# Revit family: Elite_Sliding_Window_OX_Standard
name_source: partatom
category: Windows
revit_build: Autodesk Revit 2014 (Build: 20130308_1515(x64)
units: mm (PartAtom-declared; Revit-internal decimal feet)

## types (108) — shared parameters
Centered In Wall = Yes
Custom Sash Width Left = 600 mm
Default Sill Height = 800 mm
Description = Sliding window, OX
Equal Sash Width = Yes
Frame Thickness = 70 mm
Limit Sash Height Max = 1800 mm  [stored 5.90551 ft]
Limit Sash Height Min = 300 mm
Limit Sash Width Max = 1500 mm  [stored 4.92126 ft]
Limit Sash Width Min = 300 mm
Limit Window Height Max = 1883 mm
Limit Window Height Min = 383 mm  [stored 1.25656 ft]
Limit Window Width Min = 594 mm
Manufacturer = Crealco
Model = Elite
Rough Width = 3 mm  [stored 0.00984252 ft]
Sash Frame Seal = 3 mm  [stored 0.00984252 ft]
Sash Side Spacing = 1 mm  [stored 0.00328084 ft]
URL = http://www.crealco.co.za
Wall Closure = By host
zero-valued in all types: Custom Frame Offset From Exterior

## per-type parameters (varying)
- Elite-0906OX-1000Pa: Area Left Sash Glazing=0.16 m²; Area Right Sash Glazing=0.16 m²; Clearvue SHGC Value=0.66; Clearvue U Value=5.72; Custom Windload=1000 mm  [stored 3.28084 ft]; Custom Window Height=590 mm  [stored 1.9357 ft]; Custom Window Width=890 mm  [stored 2.91995 ft]; Energy Advantage SHGC Value=0.592; Energy Advantage U Value=4.49; Height=590 mm  [stored 1.9357 ft]; Inside Heavy Duty Interlocker=No; Interlocker Configuration=0 mm  [stored 0 ft]; Intruderprufe LowE SHGC Value=0.55; Intruderprufe LowE U Value=4.31; Intruderprufe SHGC Value=0.626; Intruderprufe U Value=5.58; Limit Sash Width Left Max=596 mm; Limit Sash Width Left Min=300 mm; Limit Window Width Max=2994 mm; Max Pane Area=0.16 m²; Outside Heavy Duty Interlocker=No; Sash Height=507 mm; Sash Width Left=448 mm; Sash Width Right=448 mm; Standard Interlocker=Yes; Width=890 mm  [stored 2.91995 ft]; Windload Design=1000 mm  [stored 3.28084 ft]
- Elite-1206OX-1000Pa: Area Left Sash Glazing=0.22 m²; Area Right Sash Glazing=0.22 m²; Clearvue SHGC Value=0.675; Clearvue U Value=5.69; Custom Windload=1000 mm  [stored 3.28084 ft]; Custom Window Height=590 mm  [stored 1.9357 ft]; Custom Window Width=1190 mm  [stored 3.9042 ft]; Energy Advantage SHGC Value=0.605; Energy Advantage U Value=4.38; Height=590 mm  [stored 1.9357 ft]; Inside Heavy Duty Interlocker=No; Interlocker Configuration=0 mm  [stored 0 ft]; Intruderprufe LowE SHGC Value=0.563; Intruderprufe LowE U Value=4.22; Intruderprufe SHGC Value=0.641; Intruderprufe U Value=5.57; Limit Sash Width Left Max=896 mm; Limit Sash Width Left Min=300 mm; Limit Window Width Max=2994 mm; Max Pane Area=0.22 m²; Outside Heavy Duty Interlocker=No; Sash Height=507 mm; Sash Width Left=598 mm; Sash Width Right=598 mm; Standard Interlocker=Yes; Width=1190 mm  [stored 3.9042 ft]; Windload Design=1000 mm  [stored 3.28084 ft]
- Elite-1506OX-1000Pa: Area Left Sash Glazing=0.28 m²; Area Right Sash Glazing=0.28 m²; Clearvue SHGC Value=0.684; Clearvue U Value=5.68; Custom Windload=1000 mm  [stored 3.28084 ft]; Custom Window Height=590 mm  [stored 1.9357 ft]; Custom Window Width=1490 mm  [stored 4.88845 ft]; Energy Advantage SHGC Value=0.613; Energy Advantage U Value=4.31; Height=590 mm  [stored 1.9357 ft]; Inside Heavy Duty Interlocker=No; Interlocker Configuration=0 mm  [stored 0 ft]; Intruderprufe LowE SHGC Value=0.57; Intruderprufe LowE U Value=4.17; Intruderprufe SHGC Value=0.649; Intruderprufe U Value=5.56; Limit Sash Width Left Max=1196 mm; Limit Sash Width Left Min=300 mm; Limit Window Width Max=2994 mm; Max Pane Area=0.28 m²; Outside Heavy Duty Interlocker=No; Sash Height=507 mm; Sash Width Left=748 mm; Sash Width Right=748 mm; Standard Interlocker=Yes; Width=1490 mm  [stored 4.88845 ft]; Windload Design=1000 mm  [stored 3.28084 ft]
- Elite-1806OX-1000Pa: Area Left Sash Glazing=0.35 m²; Area Right Sash Glazing=0.35 m²; Clearvue SHGC Value=0.691; Clearvue U Value=5.67; Custom Windload=1000 mm  [stored 3.28084 ft]; Custom Window Height=590 mm  [stored 1.9357 ft]; Custom Window Width=1790 mm  [stored 5.8727 ft]; Energy Advantage SHGC Value=0.618; Energy Advantage U Value=4.27; Height=590 mm  [stored 1.9357 ft]; Inside Heavy Duty Interlocker=No; Interlocker Configuration=0 mm  [stored 0 ft]; Intruderprufe LowE SHGC Value=0.575; Intruderprufe LowE U Value=4.14; Intruderprufe SHGC Value=0.655; Intruderprufe U Value=5.55; Limit Sash Width Left Max=1496 mm; Limit Sash Width Left Min=300 mm; Limit Window Width Max=2994 mm; Max Pane Area=0.35 m²; Outside Heavy Duty Interlocker=No; Sash Height=507 mm; Sash Width Left=898 mm; Sash Width Right=898 mm; Standard Interlocker=Yes; Width=1790 mm  [stored 5.8727 ft]; Windload Design=1000 mm  [stored 3.28084 ft]
- Elite-2106OX-1000Pa: Area Left Sash Glazing=0.41 m²; Area Right Sash Glazing=0.41 m²; Clearvue SHGC Value=0.695; Clearvue U Value=5.67; Custom Windload=1000 mm  [stored 3.28084 ft]; Custom Window Height=590 mm  [stored 1.9357 ft]; Custom Window Width=2090 mm  [stored 6.85696 ft]; Energy Advantage SHGC Value=0.622; Energy Advantage U Value=4.24; Height=590 mm  [stored 1.9357 ft]; Inside Heavy Duty Interlocker=No; Interlocker Configuration=0 mm  [stored 0 ft]; Intruderprufe LowE SHGC Value=0.579; Intruderprufe LowE U Value=4.12; Intruderprufe SHGC Value=0.659; Intruderprufe U Value=5.55; Limit Sash Width Left Max=1500 mm  [stored 4.92126 ft]; Limit Sash Width Left Min=596 mm; Limit Window Width Max=2994 mm; Max Pane Area=0.41 m²; Outside Heavy Duty Interlocker=No; Sash Height=507 mm; Sash Width Left=1048 mm; Sash Width Right=1048 mm; Standard Interlocker=Yes; Width=2090 mm  [stored 6.85696 ft]; Windload Design=1000 mm  [stored 3.28084 ft]
- Elite-2406OX-1000Pa: Area Left Sash Glazing=0.47 m²; Area Right Sash Glazing=0.47 m²; Clearvue SHGC Value=0.698; Clearvue U Value=5.66; Custom Windload=1000 mm  [stored 3.28084 ft]; Custom Window Height=590 mm  [stored 1.9357 ft]; Custom Window Width=2390 mm  [stored 7.84121 ft]; Energy Advantage SHGC Value=0.625; Energy Advantage U Value=4.22; Height=590 mm  [stored 1.9357 ft]; Inside Heavy Duty Interlocker=No; Interlocker Configuration=0 mm  [stored 0 ft]; Intruderprufe LowE SHGC Value=0.582; Intruderprufe LowE U Value=4.1; Intruderprufe SHGC Value=0.662; Intruderprufe U Value=5.55; Limit Sash Width Left Max=1500 mm  [stored 4.92126 ft]; Limit Sash Width Left Min=896 mm; Limit Window Width Max=2994 mm; Max Pane Area=0.47 m²; Outside Heavy Duty Interlocker=No; Sash Height=507 mm; Sash Width Left=1198 mm; Sash Width Right=1198 mm; Standard Interlocker=Yes; Width=2390 mm  [stored 7.84121 ft]; Windload Design=1000 mm  [stored 3.28084 ft]
- Elite-2706OX-1000Pa: Area Left Sash Glazing=0.53 m²; Area Right Sash Glazing=0.53 m²; Clearvue SHGC Value=0.701; Clearvue U Value=5.66; Custom Windload=1000 mm  [stored 3.28084 ft]; Custom Window Height=590 mm  [stored 1.9357 ft]; Custom Window Width=2690 mm  [stored 8.82546 ft]; Energy Advantage SHGC Value=0.627; Energy Advantage U Value=4.2; Height=590 mm  [stored 1.9357 ft]; Inside Heavy Duty Interlocker=No; Interlocker Configuration=0 mm  [stored 0 ft]; Intruderprufe LowE SHGC Value=0.584; Intruderprufe LowE U Value=4.09; Intruderprufe SHGC Value=0.665; Intruderprufe U Value=5.54; Limit Sash Width Left Max=1500 mm  [stored 4.92126 ft]; Limit Sash Width Left Min=1196 mm; Limit Window Width Max=2994 mm; Max Pane Area=0.53 m²; Outside Heavy Duty Interlocker=No; Sash Height=507 mm; Sash Width Left=1348 mm; Sash Width Right=1348 mm; Standard Interlocker=Yes; Width=2690 mm  [stored 8.82546 ft]; Windload Design=1000 mm  [stored 3.28084 ft]
- Elite-3006OX-1000Pa: Area Left Sash Glazing=0.6 m²; Area Right Sash Glazing=0.6 m²; Clearvue SHGC Value=0.703; Clearvue U Value=5.66; Custom Windload=1000 mm  [stored 3.28084 ft]; Custom Window Height=590 mm  [stored 1.9357 ft]; Custom Window Width=2990 mm; Energy Advantage SHGC Value=0.629; Energy Advantage U Value=4.18; Height=590 mm  [stored 1.9357 ft]; Inside Heavy Duty Interlocker=No; Interlocker Configuration=0 mm  [stored 0 ft]; Intruderprufe LowE SHGC Value=0.585; Intruderprufe LowE U Value=4.08; Intruderprufe SHGC Value=0.667; Intruderprufe U Value=5.54; Limit Sash Width Left Max=1500 mm  [stored 4.92126 ft]; Limit Sash Width Left Min=1496 mm; Limit Window Width Max=2994 mm; Max Pane Area=0.6 m²; Outside Heavy Duty Interlocker=No; Sash Height=507 mm; Sash Width Left=1498 mm; Sash Width Right=1498 mm; Standard Interlocker=Yes; Width=2990 mm; Windload Design=1000 mm  [stored 3.28084 ft]
- Elite-0909OX-1000Pa: Area Left Sash Glazing=0.28 m²; Area Right Sash Glazing=0.28 m²; Clearvue SHGC Value=0.696; Clearvue U Value=5.82; Custom Windload=1000 mm  [stored 3.28084 ft]; Custom Window Height=890 mm  [stored 2.91995 ft]; Custom Window Width=890 mm  [stored 2.91995 ft]; Energy Advantage SHGC Value=0.624; Energy Advantage U Value=4.43; Height=890 mm  [stored 2.91995 ft]; Inside Heavy Duty Interlocker=No; Interlocker Configuration=0 mm  [stored 0 ft]; Intruderprufe LowE SHGC Value=0.58; Intruderprufe LowE U Value=4.25; Intruderprufe SHGC Value=0.66; Intruderprufe U Value=5.68; Limit Sash Width Left Max=596 mm; Limit Sash Width Left Min=300 mm; Limit Window Width Max=2994 mm; Max Pane Area=0.28 m²; Outside Heavy Duty Interlocker=No; Sash Height=807 mm  [stored 2.64764 ft]; Sash Width Left=448 mm; Sash Width Right=448 mm; Standard Interlocker=Yes; Width=890 mm  [stored 2.91995 ft]; Windload Design=1000 mm  [stored 3.28084 ft]
- Elite-1209OX-1000Pa: Area Left Sash Glazing=0.38 m²; Area Right Sash Glazing=0.38 m²; Clearvue SHGC Value=0.713; Clearvue U Value=5.79; Custom Windload=1000 mm  [stored 3.28084 ft]; Custom Window Height=890 mm  [stored 2.91995 ft]; Custom Window Width=1190 mm  [stored 3.9042 ft]; Energy Advantage SHGC Value=0.639; Energy Advantage U Value=4.31; Height=890 mm  [stored 2.91995 ft]; Inside Heavy Duty Interlocker=No; Interlocker Configuration=0 mm  [stored 0 ft]; Intruderprufe LowE SHGC Value=0.594; Intruderprufe LowE U Value=4.15; Intruderprufe SHGC Value=0.676; Intruderprufe U Value=5.66; Limit Sash Width Left Max=896 mm; Limit Sash Width Left Min=300 mm; Limit Window Width Max=2994 mm; Max Pane Area=0.38 m²; Outside Heavy Duty Interlocker=No; Sash Height=807 mm  [stored 2.64764 ft]; Sash Width Left=598 mm; Sash Width Right=598 mm; Standard Interlocker=Yes; Width=1190 mm  [stored 3.9042 ft]; Windload Design=1000 mm  [stored 3.28084 ft]
- Elite-1509OX-1000Pa: Area Left Sash Glazing=0.49 m²; Area Right Sash Glazing=0.49 m²; Clearvue SHGC Value=0.723; Clearvue U Value=5.78; Custom Windload=1000 mm  [stored 3.28084 ft]; Custom Window Height=890 mm  [stored 2.91995 ft]; Custom Window Width=1490 mm  [stored 4.88845 ft]; Energy Advantage SHGC Value=0.648; Energy Advantage U Value=4.23; Height=890 mm  [stored 2.91995 ft]; Inside Heavy Duty Interlocker=No; Interlocker Configuration=0 mm  [stored 0 ft]; Intruderprufe LowE SHGC Value=0.602; Intruderprufe LowE U Value=4.09; Intruderprufe SHGC Value=0.686; Intruderprufe U Value=5.65; Limit Sash Width Left Max=1196 mm; Limit Sash Width Left Min=300 mm; Limit Window Width Max=2994 mm; Max Pane Area=0.49 m²; Outside Heavy Duty Interlocker=No; Sash Height=807 mm  [stored 2.64764 ft]; Sash Width Left=748 mm; Sash Width Right=748 mm; Standard Interlocker=Yes; Width=1490 mm  [stored 4.88845 ft]; Windload Design=1000 mm  [stored 3.28084 ft]
- Elite-1809OX-1000Pa: Area Left Sash Glazing=0.6 m²; Area Right Sash Glazing=0.6 m²; Clearvue SHGC Value=0.73; Clearvue U Value=5.77; Custom Windload=1000 mm  [stored 3.28084 ft]; Custom Window Height=890 mm  [stored 2.91995 ft]; Custom Window Width=1790 mm  [stored 5.8727 ft]; Energy Advantage SHGC Value=0.654; Energy Advantage U Value=4.18; Height=890 mm  [stored 2.91995 ft]; Inside Heavy Duty Interlocker=No; Interlocker Configuration=0 mm  [stored 0 ft]; Intruderprufe LowE SHGC Value=0.608; Intruderprufe LowE U Value=4.05; Intruderprufe SHGC Value=0.696; Intruderprufe U Value=5.64; Limit Sash Width Left Max=1496 mm; Limit Sash Width Left Min=300 mm; Limit Window Width Max=2994 mm; Max Pane Area=0.6 m²; Outside Heavy Duty Interlocker=No; Sash Height=807 mm  [stored 2.64764 ft]; Sash Width Left=898 mm; Sash Width Right=898 mm; Standard Interlocker=Yes; Width=1790 mm  [stored 5.8727 ft]; Windload Design=1000 mm  [stored 3.28084 ft]
- Elite-2109OX-1000Pa: Area Left Sash Glazing=0.7 m²; Area Right Sash Glazing=0.7 m²; Clearvue SHGC Value=0.735; Clearvue U Value=5.76; Custom Windload=1000 mm  [stored 3.28084 ft]; Custom Window Height=890 mm  [stored 2.91995 ft]; Custom Window Width=2090 mm  [stored 6.85696 ft]; Energy Advantage SHGC Value=0.658; Energy Advantage U Value=4.15; Height=890 mm  [stored 2.91995 ft]; Inside Heavy Duty Interlocker=No; Interlocker Configuration=0 mm  [stored 0 ft]; Intruderprufe LowE SHGC Value=0.612; Intruderprufe LowE U Value=4.03; Intruderprufe SHGC Value=0.697; Intruderprufe U Value=5.63; Limit Sash Width Left Max=1500 mm  [stored 4.92126 ft]; Limit Sash Width Left Min=596 mm; Limit Window Width Max=2994 mm; Max Pane Area=0.7 m²; Outside Heavy Duty Interlocker=No; Sash Height=807 mm  [stored 2.64764 ft]; Sash Width Left=1048 mm; Sash Width Right=1048 mm; Standard Interlocker=Yes; Width=2090 mm  [stored 6.85696 ft]; Windload Design=1000 mm  [stored 3.28084 ft]
- Elite-2409OX-1000Pa: Area Left Sash Glazing=0.81 m²; Area Right Sash Glazing=0.81 m²; Clearvue SHGC Value=0.739; Clearvue U Value=5.75; Custom Windload=1000 mm  [stored 3.28084 ft]; Custom Window Height=890 mm  [stored 2.91995 ft]; Custom Window Width=2390 mm  [stored 7.84121 ft]; Energy Advantage SHGC Value=0.661; Energy Advantage U Value=4.12; Height=890 mm  [stored 2.91995 ft]; Inside Heavy Duty Interlocker=No; Interlocker Configuration=0 mm  [stored 0 ft]; Intruderprufe LowE SHGC Value=0.615; Intruderprufe LowE U Value=4; Intruderprufe SHGC Value=0.701; Intruderprufe U Value=5.63; Limit Sash Width Left Max=1500 mm  [stored 4.92126 ft]; Limit Sash Width Left Min=896 mm; Limit Window Width Max=2994 mm; Max Pane Area=0.81 m²; Outside Heavy Duty Interlocker=No; Sash Height=807 mm  [stored 2.64764 ft]; Sash Width Left=1198 mm; Sash Width Right=1198 mm; Standard Interlocker=Yes; Width=2390 mm  [stored 7.84121 ft]; Windload Design=1000 mm  [stored 3.28084 ft]
- Elite-2709OX-1000Pa: Area Left Sash Glazing=0.92 m²; Area Right Sash Glazing=0.92 m²; Clearvue SHGC Value=0.742; Clearvue U Value=5.75; Custom Windload=1000 mm  [stored 3.28084 ft]; Custom Window Height=890 mm  [stored 2.91995 ft]; Custom Window Width=2690 mm  [stored 8.82546 ft]; Energy Advantage SHGC Value=0.664; Energy Advantage U Value=4.1; Height=890 mm  [stored 2.91995 ft]; Inside Heavy Duty Interlocker=No; Interlocker Configuration=0 mm  [stored 0 ft]; Intruderprufe LowE SHGC Value=0.617; Intruderprufe LowE U Value=3.99; Intruderprufe SHGC Value=0.704; Intruderprufe U Value=5.62; Limit Sash Width Left Max=1500 mm  [stored 4.92126 ft]; Limit Sash Width Left Min=1196 mm; Limit Window Width Max=2994 mm; Max Pane Area=0.92 m²; Outside Heavy Duty Interlocker=No; Sash Height=807 mm  [stored 2.64764 ft]; Sash Width Left=1348 mm; Sash Width Right=1348 mm; Standard Interlocker=Yes; Width=2690 mm  [stored 8.82546 ft]; Windload Design=1000 mm  [stored 3.28084 ft]
- Elite-3009OX-1000Pa: Area Left Sash Glazing=1.03 m²; Area Right Sash Glazing=1.03 m²; Clearvue SHGC Value=0.744; Clearvue U Value=5.75; Custom Windload=1000 mm  [stored 3.28084 ft]; Custom Window Height=890 mm  [stored 2.91995 ft]; Custom Window Width=2990 mm; Energy Advantage SHGC Value=0.66; Energy Advantage U Value=4.08; Height=890 mm  [stored 2.91995 ft]; Inside Heavy Duty Interlocker=No; Interlocker Configuration=0 mm  [stored 0 ft]; Intruderprufe LowE SHGC Value=0.619; Intruderprufe LowE U Value=3.98; Intruderprufe SHGC Value=0.706; Intruderprufe U Value=5.62; Limit Sash Width Left Max=1500 mm  [stored 4.92126 ft]; Limit Sash Width Left Min=1496 mm; Limit Window Width Max=2994 mm; Max Pane Area=1.03 m²; Outside Heavy Duty Interlocker=No; Sash Height=807 mm  [stored 2.64764 ft]; Sash Width Left=1498 mm; Sash Width Right=1498 mm; Standard Interlocker=Yes; Width=2990 mm; Windload Design=1000 mm  [stored 3.28084 ft]
- Elite-0912OX-1000Pa: Area Left Sash Glazing=0.39 m²; Area Right Sash Glazing=0.39 m²; Clearvue SHGC Value=0.714; Clearvue U Value=5.86; Custom Windload=1000 mm  [stored 3.28084 ft]; Custom Window Height=1190 mm  [stored 3.9042 ft]; Custom Window Width=890 mm  [stored 2.91995 ft]; Energy Advantage SHGC Value=0.639; Energy Advantage U Value=4.4; Height=1190 mm  [stored 3.9042 ft]; Inside Heavy Duty Interlocker=No; Interlocker Configuration=0 mm  [stored 0 ft]; Intruderprufe LowE SHGC Value=0.594; Intruderprufe LowE U Value=4.22; Intruderprufe SHGC Value=0.677; Intruderprufe U Value=5.72; Limit Sash Width Left Max=596 mm; Limit Sash Width Left Min=300 mm; Limit Window Width Max=2994 mm; Max Pane Area=0.39 m²; Outside Heavy Duty Interlocker=No; Sash Height=1107 mm  [stored 3.63189 ft]; Sash Width Left=448 mm; Sash Width Right=448 mm; Standard Interlocker=Yes; Width=890 mm  [stored 2.91995 ft]; Windload Design=1000 mm  [stored 3.28084 ft]
- Elite-1212OX-1000Pa: Area Left Sash Glazing=0.54 m²; Area Right Sash Glazing=0.54 m²; Clearvue SHGC Value=0.732; Clearvue U Value=5.84; Custom Windload=1000 mm  [stored 3.28084 ft]; Custom Window Height=1190 mm  [stored 3.9042 ft]; Custom Window Width=1190 mm  [stored 3.9042 ft]; Energy Advantage SHGC Value=0.655; Energy Advantage U Value=4.27; Height=1190 mm  [stored 3.9042 ft]; Inside Heavy Duty Interlocker=No; Interlocker Configuration=0 mm  [stored 0 ft]; Intruderprufe LowE SHGC Value=0.609; Intruderprufe LowE U Value=4.11; Intruderprufe SHGC Value=0.694; Intruderprufe U Value=5.7; Limit Sash Width Left Max=896 mm; Limit Sash Width Left Min=300 mm; Limit Window Width Max=2994 mm; Max Pane Area=0.54 m²; Outside Heavy Duty Interlocker=No; Sash Height=1107 mm  [stored 3.63189 ft]; Sash Width Left=598 mm; Sash Width Right=598 mm; Standard Interlocker=Yes; Width=1190 mm  [stored 3.9042 ft]; Windload Design=1000 mm  [stored 3.28084 ft]
- Elite-1512OX-1000Pa: Area Left Sash Glazing=0.7 m²; Area Right Sash Glazing=0.7 m²; Clearvue SHGC Value=0.743; Clearvue U Value=5.82; Custom Windload=1000 mm  [stored 3.28084 ft]; Custom Window Height=1190 mm  [stored 3.9042 ft]; Custom Window Width=1490 mm  [stored 4.88845 ft]; Energy Advantage SHGC Value=0.665; Energy Advantage U Value=4.19; Height=1190 mm  [stored 3.9042 ft]; Inside Heavy Duty Interlocker=No; Interlocker Configuration=0 mm  [stored 0 ft]; Intruderprufe LowE SHGC Value=0.618; Intruderprufe LowE U Value=4.05; Intruderprufe SHGC Value=0.704; Intruderprufe U Value=5.69; Limit Sash Width Left Max=1196 mm; Limit Sash Width Left Min=300 mm; Limit Window Width Max=2994 mm; Max Pane Area=0.7 m²; Outside Heavy Duty Interlocker=No; Sash Height=1107 mm  [stored 3.63189 ft]; Sash Width Left=748 mm; Sash Width Right=748 mm; Standard Interlocker=Yes; Width=1490 mm  [stored 4.88845 ft]; Windload Design=1000 mm  [stored 3.28084 ft]
- Elite-1812OX-1000Pa: Area Left Sash Glazing=0.85 m²; Area Right Sash Glazing=0.85 m²; Clearvue SHGC Value=0.75; Clearvue U Value=5.81; Custom Windload=1000 mm  [stored 3.28084 ft]; Custom Window Height=1190 mm  [stored 3.9042 ft]; Custom Window Width=1790 mm  [stored 5.8727 ft]; Energy Advantage SHGC Value=0.671; Energy Advantage U Value=4.14; Height=1190 mm  [stored 3.9042 ft]; Inside Heavy Duty Interlocker=No; Interlocker Configuration=0 mm  [stored 0 ft]; Intruderprufe LowE SHGC Value=0.624; Intruderprufe LowE U Value=4.01; Intruderprufe SHGC Value=0.711; Intruderprufe U Value=5.68; Limit Sash Width Left Max=1496 mm; Limit Sash Width Left Min=300 mm; Limit Window Width Max=2994 mm; Max Pane Area=0.85 m²; Outside Heavy Duty Interlocker=No; Sash Height=1107 mm  [stored 3.63189 ft]; Sash Width Left=898 mm; Sash Width Right=898 mm; Standard Interlocker=Yes; Width=1790 mm  [stored 5.8727 ft]; Windload Design=1000 mm  [stored 3.28084 ft]
- Elite-2112OX-1000Pa: Area Left Sash Glazing=1 m²; Area Right Sash Glazing=1 m²; Clearvue SHGC Value=0.755; Clearvue U Value=5.8; Custom Windload=1000 mm  [stored 3.28084 ft]; Custom Window Height=1190 mm  [stored 3.9042 ft]; Custom Window Width=2090 mm  [stored 6.85696 ft]; Energy Advantage SHGC Value=0.676; Energy Advantage U Value=4.1; Height=1190 mm  [stored 3.9042 ft]; Inside Heavy Duty Interlocker=No; Interlocker Configuration=0 mm  [stored 0 ft]; Intruderprufe LowE SHGC Value=0.628; Intruderprufe LowE U Value=3.98; Intruderprufe SHGC Value=0.716; Intruderprufe U Value=5.67; Limit Sash Width Left Max=1500 mm  [stored 4.92126 ft]; Limit Sash Width Left Min=596 mm; Limit Window Width Max=2994 mm; Max Pane Area=1 m²; Outside Heavy Duty Interlocker=No; Sash Height=1107 mm  [stored 3.63189 ft]; Sash Width Left=1048 mm; Sash Width Right=1048 mm; Standard Interlocker=Yes; Width=2090 mm  [stored 6.85696 ft]; Windload Design=1000 mm  [stored 3.28084 ft]
- Elite-2412OX-1000Pa: Area Left Sash Glazing=1.15 m²; Area Right Sash Glazing=1.15 m²; Clearvue SHGC Value=0.759; Clearvue U Value=5.8; Custom Windload=1000 mm  [stored 3.28084 ft]; Custom Window Height=1190 mm  [stored 3.9042 ft]; Custom Window Width=2390 mm  [stored 7.84121 ft]; Energy Advantage SHGC Value=0.679; Energy Advantage U Value=4.07; Height=1190 mm  [stored 3.9042 ft]; Inside Heavy Duty Interlocker=No; Interlocker Configuration=0 mm  [stored 0 ft]; Intruderprufe LowE SHGC Value=0.631; Intruderprufe LowE U Value=3.96; Intruderprufe SHGC Value=0.72; Intruderprufe U Value=5.67; Limit Sash Width Left Max=1500 mm  [stored 4.92126 ft]; Limit Sash Width Left Min=896 mm; Limit Window Width Max=2994 mm; Max Pane Area=1.15 m²; Outside Heavy Duty Interlocker=No; Sash Height=1107 mm  [stored 3.63189 ft]; Sash Width Left=1198 mm; Sash Width Right=1198 mm; Standard Interlocker=Yes; Width=2390 mm  [stored 7.84121 ft]; Windload Design=1000 mm  [stored 3.28084 ft]
- Elite-2712OX-1000Pa: Area Left Sash Glazing=1.31 m²; Area Right Sash Glazing=1.31 m²; Clearvue SHGC Value=0.762; Clearvue U Value=5.79; Custom Windload=1000 mm  [stored 3.28084 ft]; Custom Window Height=1190 mm  [stored 3.9042 ft]; Custom Window Width=2690 mm  [stored 8.82546 ft]; Energy Advantage SHGC Value=0.682; Energy Advantage U Value=4.05; Height=1190 mm  [stored 3.9042 ft]; Inside Heavy Duty Interlocker=No; Interlocker Configuration=0 mm  [stored 0 ft]; Intruderprufe LowE SHGC Value=0.634; Intruderprufe LowE U Value=3.94; Intruderprufe SHGC Value=0.723; Intruderprufe U Value=5.67; Limit Sash Width Left Max=1500 mm  [stored 4.92126 ft]; Limit Sash Width Left Min=1196 mm; Limit Window Width Max=2994 mm; Max Pane Area=1.31 m²; Outside Heavy Duty Interlocker=No; Sash Height=1107 mm  [stored 3.63189 ft]; Sash Width Left=1348 mm; Sash Width Right=1348 mm; Standard Interlocker=Yes; Width=2690 mm  [stored 8.82546 ft]; Windload Design=1000 mm  [stored 3.28084 ft]
- Elite-3012OX-1000Pa: Area Left Sash Glazing=1.46 m²; Area Right Sash Glazing=1.46 m²; Clearvue SHGC Value=0.764; Clearvue U Value=5.79; Custom Windload=1000 mm  [stored 3.28084 ft]; Custom Window Height=1190 mm  [stored 3.9042 ft]; Custom Window Width=2990 mm; Energy Advantage SHGC Value=0.684; Energy Advantage U Value=4.03; Height=1190 mm  [stored 3.9042 ft]; Inside Heavy Duty Interlocker=Yes; Interlocker Configuration=1 mm  [stored 0.00328084 ft]; Intruderprufe LowE SHGC Value=0.636; Intruderprufe LowE U Value=3.93; Intruderprufe SHGC Value=0.725; Intruderprufe U Value=5.66; Limit Sash Width Left Max=1500 mm  [stored 4.92126 ft]; Limit Sash Width Left Min=1496 mm; Limit Window Width Max=2994 mm; Max Pane Area=1.46 m²; Outside Heavy Duty Interlocker=No; Sash Height=1107 mm  [stored 3.63189 ft]; Sash Width Left=1498 mm; Sash Width Right=1498 mm; Standard Interlocker=No; Width=2990 mm; Windload Design=1000 mm  [stored 3.28084 ft]
- Elite-0915OX-1000Pa: Area Left Sash Glazing=0.51 m²; Area Right Sash Glazing=0.51 m²; Clearvue SHGC Value=0.724; Clearvue U Value=5.89; Custom Windload=1000 mm  [stored 3.28084 ft]; Custom Window Height=1490 mm  [stored 4.88845 ft]; Custom Window Width=890 mm  [stored 2.91995 ft]; Energy Advantage SHGC Value=0.649; Energy Advantage U Value=4.39; Height=1490 mm  [stored 4.88845 ft]; Inside Heavy Duty Interlocker=No; Interlocker Configuration=0 mm  [stored 0 ft]; Intruderprufe LowE SHGC Value=0.603; Intruderprufe LowE U Value=4.2; Intruderprufe SHGC Value=0.687; Intruderprufe U Value=5.75; Limit Sash Width Left Max=596 mm; Limit Sash Width Left Min=300 mm; Limit Window Width Max=2994 mm; Max Pane Area=0.51 m²; Outside Heavy Duty Interlocker=No; Sash Height=1407 mm  [stored 4.61614 ft]; Sash Width Left=448 mm; Sash Width Right=448 mm; Standard Interlocker=Yes; Width=890 mm  [stored 2.91995 ft]; Windload Design=1000 mm  [stored 3.28084 ft]
- Elite-1215OX-1000Pa: Area Left Sash Glazing=0.7 m²; Area Right Sash Glazing=0.7 m²; Clearvue SHGC Value=0.743; Clearvue U Value=5.87; Custom Windload=1000 mm  [stored 3.28084 ft]; Custom Window Height=1490 mm  [stored 4.88845 ft]; Custom Window Width=1190 mm  [stored 3.9042 ft]; Energy Advantage SHGC Value=0.665; Energy Advantage U Value=4.25; Height=1490 mm  [stored 4.88845 ft]; Inside Heavy Duty Interlocker=Yes; Interlocker Configuration=1 mm  [stored 0.00328084 ft]; Intruderprufe LowE SHGC Value=0.618; Intruderprufe LowE U Value=4.09; Intruderprufe SHGC Value=0.705; Intruderprufe U Value=5.73; Limit Sash Width Left Max=896 mm; Limit Sash Width Left Min=300 mm; Limit Window Width Max=2994 mm; Max Pane Area=0.7 m²; Outside Heavy Duty Interlocker=No; Sash Height=1407 mm  [stored 4.61614 ft]; Sash Width Left=598 mm; Sash Width Right=598 mm; Standard Interlocker=No; Width=1190 mm  [stored 3.9042 ft]; Windload Design=1000 mm  [stored 3.28084 ft]
- Elite-1515OX-1000Pa: Area Left Sash Glazing=0.9 m²; Area Right Sash Glazing=0.9 m²; Clearvue SHGC Value=0.755; Clearvue U Value=5.95; Custom Windload=1000 mm  [stored 3.28084 ft]; Custom Window Height=1490 mm  [stored 4.88845 ft]; Custom Window Width=1490 mm  [stored 4.88845 ft]; Energy Advantage SHGC Value=0.676; Energy Advantage U Value=4.27; Height=1490 mm  [stored 4.88845 ft]; Inside Heavy Duty Interlocker=Yes; Interlocker Configuration=1 mm  [stored 0.00328084 ft]; Intruderprufe LowE SHGC Value=0.628; Intruderprufe LowE U Value=4.13; Intruderprufe SHGC Value=0.7163; Intruderprufe U Value=5.82; Limit Sash Width Left Max=1196 mm; Limit Sash Width Left Min=300 mm; Limit Window Width Max=2994 mm; Max Pane Area=0.9 m²; Outside Heavy Duty Interlocker=No; Sash Height=1407 mm  [stored 4.61614 ft]; Sash Width Left=748 mm; Sash Width Right=748 mm; Standard Interlocker=No; Width=1490 mm  [stored 4.88845 ft]; Windload Design=1000 mm  [stored 3.28084 ft]
- Elite-1815OX-1000Pa: Area Left Sash Glazing=1.1 m²; Area Right Sash Glazing=1.1 m²; Clearvue SHGC Value=0.762; Clearvue U Value=5.84; Custom Windload=1000 mm  [stored 3.28084 ft]; Custom Window Height=1490 mm  [stored 4.88845 ft]; Custom Window Width=1790 mm  [stored 5.8727 ft]; Energy Advantage SHGC Value=0.682; Energy Advantage U Value=4.11; Height=1490 mm  [stored 4.88845 ft]; Inside Heavy Duty Interlocker=Yes; Interlocker Configuration=1 mm  [stored 0.00328084 ft]; Intruderprufe LowE SHGC Value=0.633; Intruderprufe LowE U Value=3.98; Intruderprufe SHGC Value=0.722; Intruderprufe U Value=5.71; Limit Sash Width Left Max=1496 mm; Limit Sash Width Left Min=300 mm; Limit Window Width Max=2994 mm; Max Pane Area=1.1 m²; Outside Heavy Duty Interlocker=No; Sash Height=1407 mm  [stored 4.61614 ft]; Sash Width Left=898 mm; Sash Width Right=898 mm; Standard Interlocker=No; Width=1790 mm  [stored 5.8727 ft]; Windload Design=1000 mm  [stored 3.28084 ft]
- Elite-2115OX-1000Pa: Area Left Sash Glazing=1.3 m²; Area Right Sash Glazing=1.3 m²; Clearvue SHGC Value=0.767; Clearvue U Value=5.83; Custom Windload=1000 mm  [stored 3.28084 ft]; Custom Window Height=1490 mm  [stored 4.88845 ft]; Custom Window Width=2090 mm  [stored 6.85696 ft]; Energy Advantage SHGC Value=0.686; Energy Advantage U Value=4.07; Height=1490 mm  [stored 4.88845 ft]; Inside Heavy Duty Interlocker=Yes; Interlocker Configuration=1 mm  [stored 0.00328084 ft]; Intruderprufe LowE SHGC Value=0.638; Intruderprufe LowE U Value=3.95; Intruderprufe SHGC Value=0.727; Intruderprufe U Value=5.7; Limit Sash Width Left Max=1500 mm  [stored 4.92126 ft]; Limit Sash Width Left Min=596 mm; Limit Window Width Max=2994 mm; Max Pane Area=1.3 m²; Outside Heavy Duty Interlocker=No; Sash Height=1407 mm  [stored 4.61614 ft]; Sash Width Left=1048 mm; Sash Width Right=1048 mm; Standard Interlocker=No; Width=2090 mm  [stored 6.85696 ft]; Windload Design=1000 mm  [stored 3.28084 ft]
- Elite-2415OX-1000Pa: Area Left Sash Glazing=1.49 m²; Area Right Sash Glazing=1.49 m²; Clearvue SHGC Value=0.771; Clearvue U Value=5.82; Custom Windload=1000 mm  [stored 3.28084 ft]; Custom Window Height=1490 mm  [stored 4.88845 ft]; Custom Window Width=2390 mm  [stored 7.84121 ft]; Energy Advantage SHGC Value=0.69; Energy Advantage U Value=4.05; Height=1490 mm  [stored 4.88845 ft]; Inside Heavy Duty Interlocker=Yes; Interlocker Configuration=1 mm  [stored 0.00328084 ft]; Intruderprufe LowE SHGC Value=0.641; Intruderprufe LowE U Value=3.93; Intruderprufe SHGC Value=0.731; Intruderprufe U Value=5.69; Limit Sash Width Left Max=1500 mm  [stored 4.92126 ft]; Limit Sash Width Left Min=896 mm; Limit Window Width Max=2994 mm; Max Pane Area=1.49 m²; Outside Heavy Duty Interlocker=No; Sash Height=1407 mm  [stored 4.61614 ft]; Sash Width Left=1198 mm; Sash Width Right=1198 mm; Standard Interlocker=No; Width=2390 mm  [stored 7.84121 ft]; Windload Design=1000 mm  [stored 3.28084 ft]
- Elite-2715OX-1000Pa: Area Left Sash Glazing=1.69 m²; Area Right Sash Glazing=1.69 m²; Clearvue SHGC Value=0.774; Clearvue U Value=5.82; Custom Windload=1000 mm  [stored 3.28084 ft]; Custom Window Height=1490 mm  [stored 4.88845 ft]; Custom Window Width=2690 mm  [stored 8.82546 ft]; Energy Advantage SHGC Value=0.692; Energy Advantage U Value=4.02; Height=1490 mm  [stored 4.88845 ft]; Inside Heavy Duty Interlocker=Yes; Interlocker Configuration=1 mm  [stored 0.00328084 ft]; Intruderprufe LowE SHGC Value=0.643; Intruderprufe LowE U Value=3.91; Intruderprufe SHGC Value=0.734; Intruderprufe U Value=5.69; Limit Sash Width Left Max=1500 mm  [stored 4.92126 ft]; Limit Sash Width Left Min=1196 mm; Limit Window Width Max=2994 mm; Max Pane Area=1.69 m²; Outside Heavy Duty Interlocker=No; Sash Height=1407 mm  [stored 4.61614 ft]; Sash Width Left=1348 mm; Sash Width Right=1348 mm; Standard Interlocker=No; Width=2690 mm  [stored 8.82546 ft]; Windload Design=1000 mm  [stored 3.28084 ft]
- Elite-3015OX-1000Pa: Area Left Sash Glazing=1.89 m²; Area Right Sash Glazing=1.89 m²; Clearvue SHGC Value=0.777; Clearvue U Value=5.82; Custom Windload=1000 mm  [stored 3.28084 ft]; Custom Window Height=1490 mm  [stored 4.88845 ft]; Custom Window Width=2990 mm; Energy Advantage SHGC Value=0.695; Energy Advantage U Value=4; Height=1490 mm  [stored 4.88845 ft]; Inside Heavy Duty Interlocker=Yes; Interlocker Configuration=1 mm  [stored 0.00328084 ft]; Intruderprufe LowE SHGC Value=0.645; Intruderprufe LowE U Value=3.9; Intruderprufe SHGC Value=0.737; Intruderprufe U Value=5.69; Limit Sash Width Left Max=1500 mm  [stored 4.92126 ft]; Limit Sash Width Left Min=1496 mm; Limit Window Width Max=2994 mm; Max Pane Area=1.89 m²; Outside Heavy Duty Interlocker=No; Sash Height=1407 mm  [stored 4.61614 ft]; Sash Width Left=1498 mm; Sash Width Right=1498 mm; Standard Interlocker=No; Width=2990 mm; Windload Design=1000 mm  [stored 3.28084 ft]
- Elite-0918OX-1000Pa: Area Left Sash Glazing=0.62 m²; Area Right Sash Glazing=0.62 m²; Clearvue SHGC Value=0.733; Clearvue U Value=6.08; Custom Windload=1000 mm  [stored 3.28084 ft]; Custom Window Height=1790 mm  [stored 5.8727 ft]; Custom Window Width=890 mm  [stored 2.91995 ft]; Energy Advantage SHGC Value=0.657; Energy Advantage U Value=4.54; Height=1790 mm  [stored 5.8727 ft]; Inside Heavy Duty Interlocker=Yes; Interlocker Configuration=1 mm  [stored 0.00328084 ft]; Intruderprufe LowE SHGC Value=0.611; Intruderprufe LowE U Value=4.37; Intruderprufe SHGC Value=0.695; Intruderprufe U Value=5.59; Limit Sash Width Left Max=596 mm; Limit Sash Width Left Min=300 mm; Limit Window Width Max=2994 mm; Max Pane Area=0.62 m²; Outside Heavy Duty Interlocker=No; Sash Height=1707 mm; Sash Width Left=448 mm; Sash Width Right=448 mm; Standard Interlocker=No; Width=890 mm  [stored 2.91995 ft]; Windload Design=1000 mm  [stored 3.28084 ft]
- Elite-1218OX-1000Pa: Area Left Sash Glazing=0.87 m²; Area Right Sash Glazing=0.87 m²; Clearvue SHGC Value=0.751; Clearvue U Value=5.88; Custom Windload=1000 mm  [stored 3.28084 ft]; Custom Window Height=1790 mm  [stored 5.8727 ft]; Custom Window Width=1190 mm  [stored 3.9042 ft]; Energy Advantage SHGC Value=0.672; Energy Advantage U Value=4.24; Height=1790 mm  [stored 5.8727 ft]; Inside Heavy Duty Interlocker=Yes; Interlocker Configuration=1 mm  [stored 0.00328084 ft]; Intruderprufe LowE SHGC Value=0.624; Intruderprufe LowE U Value=4.08; Intruderprufe SHGC Value=0.712; Intruderprufe U Value=5.75; Limit Sash Width Left Max=896 mm; Limit Sash Width Left Min=300 mm; Limit Window Width Max=2994 mm; Max Pane Area=0.87 m²; Outside Heavy Duty Interlocker=No; Sash Height=1707 mm; Sash Width Left=598 mm; Sash Width Right=598 mm; Standard Interlocker=No; Width=1190 mm  [stored 3.9042 ft]; Windload Design=1000 mm  [stored 3.28084 ft]
- Elite-1518OX-1000Pa: Area Left Sash Glazing=1.11 m²; Area Right Sash Glazing=1.11 m²; Clearvue SHGC Value=0.762; Clearvue U Value=5.87; Custom Windload=1000 mm  [stored 3.28084 ft]; Custom Window Height=1790 mm  [stored 5.8727 ft]; Custom Window Width=1490 mm  [stored 4.88845 ft]; Energy Advantage SHGC Value=0.682; Energy Advantage U Value=4.15; Height=1790 mm  [stored 5.8727 ft]; Inside Heavy Duty Interlocker=Yes; Interlocker Configuration=2 mm  [stored 0.00656168 ft]; Intruderprufe LowE SHGC Value=0.634; Intruderprufe LowE U Value=4.01; Intruderprufe SHGC Value=0.723; Intruderprufe U Value=5.73; Limit Sash Width Left Max=1196 mm; Limit Sash Width Left Min=300 mm; Limit Window Width Max=2994 mm; Max Pane Area=1.11 m²; Outside Heavy Duty Interlocker=Yes; Sash Height=1707 mm; Sash Width Left=748 mm; Sash Width Right=748 mm; Standard Interlocker=No; Width=1490 mm  [stored 4.88845 ft]; Windload Design=1000 mm  [stored 3.28084 ft]
- Elite-1818OX-1000Pa: Area Left Sash Glazing=1.35 m²; Area Right Sash Glazing=1.35 m²; Clearvue SHGC Value=0.77; Clearvue U Value=5.86; Custom Windload=1000 mm  [stored 3.28084 ft]; Custom Window Height=1790 mm  [stored 5.8727 ft]; Custom Window Width=1790 mm  [stored 5.8727 ft]; Energy Advantage SHGC Value=0.688; Energy Advantage U Value=4.1; Height=1790 mm  [stored 5.8727 ft]; Inside Heavy Duty Interlocker=Yes; Interlocker Configuration=2 mm  [stored 0.00656168 ft]; Intruderprufe LowE SHGC Value=0.64; Intruderprufe LowE U Value=3.96; Intruderprufe SHGC Value=0.73; Intruderprufe U Value=5.72; Limit Sash Width Left Max=1496 mm; Limit Sash Width Left Min=300 mm; Limit Window Width Max=2994 mm; Max Pane Area=1.35 m²; Outside Heavy Duty Interlocker=Yes; Sash Height=1707 mm; Sash Width Left=898 mm; Sash Width Right=898 mm; Standard Interlocker=No; Width=1790 mm  [stored 5.8727 ft]; Windload Design=1000 mm  [stored 3.28084 ft]
- Elite-2118OX-1000Pa: Area Left Sash Glazing=1.59 m²; Area Right Sash Glazing=1.59 m²; Clearvue SHGC Value=0.775; Clearvue U Value=5.85; Custom Windload=1000 mm  [stored 3.28084 ft]; Custom Window Height=1790 mm  [stored 5.8727 ft]; Custom Window Width=2090 mm  [stored 6.85696 ft]; Energy Advantage SHGC Value=0.693; Energy Advantage U Value=4.06; Height=1790 mm  [stored 5.8727 ft]; Inside Heavy Duty Interlocker=Yes; Interlocker Configuration=2 mm  [stored 0.00656168 ft]; Intruderprufe LowE SHGC Value=0.644; Intruderprufe LowE U Value=3.93; Intruderprufe SHGC Value=0.735; Intruderprufe U Value=5.71; Limit Sash Width Left Max=1500 mm  [stored 4.92126 ft]; Limit Sash Width Left Min=596 mm; Limit Window Width Max=2994 mm; Max Pane Area=1.59 m²; Outside Heavy Duty Interlocker=Yes; Sash Height=1707 mm; Sash Width Left=1048 mm; Sash Width Right=1048 mm; Standard Interlocker=No; Width=2090 mm  [stored 6.85696 ft]; Windload Design=1000 mm  [stored 3.28084 ft]
- Elite-2418OX-1000Pa: Area Left Sash Glazing=1.83 m²; Area Right Sash Glazing=1.83 m²; Clearvue SHGC Value=0.779; Clearvue U Value=5.84; Custom Windload=1000 mm  [stored 3.28084 ft]; Custom Window Height=1790 mm  [stored 5.8727 ft]; Custom Window Width=2390 mm  [stored 7.84121 ft]; Energy Advantage SHGC Value=0.697; Energy Advantage U Value=4.03; Height=1790 mm  [stored 5.8727 ft]; Inside Heavy Duty Interlocker=Yes; Interlocker Configuration=2 mm  [stored 0.00656168 ft]; Intruderprufe LowE SHGC Value=0.647; Intruderprufe LowE U Value=3.91; Intruderprufe SHGC Value=0.739; Intruderprufe U Value=5.71; Limit Sash Width Left Max=1500 mm  [stored 4.92126 ft]; Limit Sash Width Left Min=896 mm; Limit Window Width Max=2994 mm; Max Pane Area=1.83 m²; Outside Heavy Duty Interlocker=Yes; Sash Height=1707 mm; Sash Width Left=1198 mm; Sash Width Right=1198 mm; Standard Interlocker=No; Width=2390 mm  [stored 7.84121 ft]; Windload Design=1000 mm  [stored 3.28084 ft]
- Elite-2718OX-1000Pa: Area Left Sash Glazing=2.08 m²; Area Right Sash Glazing=2.08 m²; Clearvue SHGC Value=0.782; Clearvue U Value=5.84; Custom Windload=1000 mm  [stored 3.28084 ft]; Custom Window Height=1790 mm  [stored 5.8727 ft]; Custom Window Width=2690 mm  [stored 8.82546 ft]; Energy Advantage SHGC Value=0.699; Energy Advantage U Value=4; Height=1790 mm  [stored 5.8727 ft]; Inside Heavy Duty Interlocker=Yes; Interlocker Configuration=2 mm  [stored 0.00656168 ft]; Intruderprufe LowE SHGC Value=0.65; Intruderprufe LowE U Value=3.89; Intruderprufe SHGC Value=0.742; Intruderprufe U Value=5.71; Limit Sash Width Left Max=1500 mm  [stored 4.92126 ft]; Limit Sash Width Left Min=1196 mm; Limit Window Width Max=2994 mm; Max Pane Area=2.08 m²; Outside Heavy Duty Interlocker=Yes; Sash Height=1707 mm; Sash Width Left=1348 mm; Sash Width Right=1348 mm; Standard Interlocker=No; Width=2690 mm  [stored 8.82546 ft]; Windload Design=1000 mm  [stored 3.28084 ft]
- Elite-3018OX-1000Pa: Area Left Sash Glazing=2.32 m²; Area Right Sash Glazing=2.32 m²; Clearvue SHGC Value=0.785; Clearvue U Value=5.83; Custom Windload=1000 mm  [stored 3.28084 ft]; Custom Window Height=1790 mm  [stored 5.8727 ft]; Custom Window Width=2990 mm; Energy Advantage SHGC Value=0.702; Energy Advantage U Value=3.99; Height=1790 mm  [stored 5.8727 ft]; Inside Heavy Duty Interlocker=Yes; Interlocker Configuration=2 mm  [stored 0.00656168 ft]; Intruderprufe LowE SHGC Value=0.652; Intruderprufe LowE U Value=3.88; Intruderprufe SHGC Value=0.744; Intruderprufe U Value=5.7; Limit Sash Width Left Max=1500 mm  [stored 4.92126 ft]; Limit Sash Width Left Min=1496 mm; Limit Window Width Max=2994 mm; Max Pane Area=2.32 m²; Outside Heavy Duty Interlocker=Yes; Sash Height=1707 mm; Sash Width Left=1498 mm; Sash Width Right=1498 mm; Standard Interlocker=No; Width=2990 mm; Windload Design=1000 mm  [stored 3.28084 ft]
- Elite-0906OX-1500Pa: Area Left Sash Glazing=0.16 m²; Area Right Sash Glazing=0.16 m²; Clearvue SHGC Value=0.66; Clearvue U Value=5.72; Custom Windload=1500 mm  [stored 4.92126 ft]; Custom Window Height=590 mm  [stored 1.9357 ft]; Custom Window Width=890 mm  [stored 2.91995 ft]; Energy Advantage SHGC Value=0.592; Energy Advantage U Value=4.49; Height=590 mm  [stored 1.9357 ft]; Inside Heavy Duty Interlocker=No; Interlocker Configuration=0 mm  [stored 0 ft]; Intruderprufe LowE SHGC Value=0.55; Intruderprufe LowE U Value=4.31; Intruderprufe SHGC Value=0.626; Intruderprufe U Value=5.58; Limit Sash Width Left Max=596 mm; Limit Sash Width Left Min=300 mm; Limit Window Width Max=2994 mm; Max Pane Area=0.16 m²; Outside Heavy Duty Interlocker=No; Sash Height=507 mm; Sash Width Left=448 mm; Sash Width Right=448 mm; Standard Interlocker=Yes; Width=890 mm  [stored 2.91995 ft]; Windload Design=1500 mm  [stored 4.92126 ft]
- Elite-0906OX-2000Pa: Area Left Sash Glazing=0.16 m²; Area Right Sash Glazing=0.16 m²; Clearvue SHGC Value=0.66; Clearvue U Value=5.72; Custom Windload=2000 mm  [stored 6.56168 ft]; Custom Window Height=590 mm  [stored 1.9357 ft]; Custom Window Width=890 mm  [stored 2.91995 ft]; Energy Advantage SHGC Value=0.592; Energy Advantage U Value=4.49; Height=590 mm  [stored 1.9357 ft]; Inside Heavy Duty Interlocker=No; Interlocker Configuration=0 mm  [stored 0 ft]; Intruderprufe LowE SHGC Value=0.55; Intruderprufe LowE U Value=4.31; Intruderprufe SHGC Value=0.626; Intruderprufe U Value=5.58; Limit Sash Width Left Max=596 mm; Limit Sash Width Left Min=300 mm; Limit Window Width Max=2994 mm; Max Pane Area=0.16 m²; Outside Heavy Duty Interlocker=No; Sash Height=507 mm; Sash Width Left=448 mm; Sash Width Right=448 mm; Standard Interlocker=Yes; Width=890 mm  [stored 2.91995 ft]; Windload Design=2000 mm  [stored 6.56168 ft]
- Elite-0909OX-1500Pa: Area Left Sash Glazing=0.28 m²; Area Right Sash Glazing=0.28 m²; Clearvue SHGC Value=0.696; Clearvue U Value=5.82; Custom Windload=1500 mm  [stored 4.92126 ft]; Custom Window Height=890 mm  [stored 2.91995 ft]; Custom Window Width=890 mm  [stored 2.91995 ft]; Energy Advantage SHGC Value=0.624; Energy Advantage U Value=4.43; Height=890 mm  [stored 2.91995 ft]; Inside Heavy Duty Interlocker=No; Interlocker Configuration=0 mm  [stored 0 ft]; Intruderprufe LowE SHGC Value=0.58; Intruderprufe LowE U Value=4.25; Intruderprufe SHGC Value=0.66; Intruderprufe U Value=5.68; Limit Sash Width Left Max=596 mm; Limit Sash Width Left Min=300 mm; Limit Window Width Max=2994 mm; Max Pane Area=0.28 m²; Outside Heavy Duty Interlocker=No; Sash Height=807 mm  [stored 2.64764 ft]; Sash Width Left=448 mm; Sash Width Right=448 mm; Standard Interlocker=Yes; Width=890 mm  [stored 2.91995 ft]; Windload Design=1500 mm  [stored 4.92126 ft]
- Elite-0909OX-2000Pa: Area Left Sash Glazing=0.28 m²; Area Right Sash Glazing=0.28 m²; Clearvue SHGC Value=0.696; Clearvue U Value=5.82; Custom Windload=2000 mm  [stored 6.56168 ft]; Custom Window Height=890 mm  [stored 2.91995 ft]; Custom Window Width=890 mm  [stored 2.91995 ft]; Energy Advantage SHGC Value=0.624; Energy Advantage U Value=4.43; Height=890 mm  [stored 2.91995 ft]; Inside Heavy Duty Interlocker=No; Interlocker Configuration=0 mm  [stored 0 ft]; Intruderprufe LowE SHGC Value=0.58; Intruderprufe LowE U Value=4.25; Intruderprufe SHGC Value=0.66; Intruderprufe U Value=5.68; Limit Sash Width Left Max=596 mm; Limit Sash Width Left Min=300 mm; Limit Window Width Max=2994 mm; Max Pane Area=0.28 m²; Outside Heavy Duty Interlocker=No; Sash Height=807 mm  [stored 2.64764 ft]; Sash Width Left=448 mm; Sash Width Right=448 mm; Standard Interlocker=Yes; Width=890 mm  [stored 2.91995 ft]; Windload Design=2000 mm  [stored 6.56168 ft]
- Elite-0912OX-1500Pa: Area Left Sash Glazing=0.39 m²; Area Right Sash Glazing=0.39 m²; Clearvue SHGC Value=0.714; Clearvue U Value=5.86; Custom Windload=1500 mm  [stored 4.92126 ft]; Custom Window Height=1190 mm  [stored 3.9042 ft]; Custom Window Width=890 mm  [stored 2.91995 ft]; Energy Advantage SHGC Value=0.639; Energy Advantage U Value=4.4; Height=1190 mm  [stored 3.9042 ft]; Inside Heavy Duty Interlocker=No; Interlocker Configuration=0 mm  [stored 0 ft]; Intruderprufe LowE SHGC Value=0.594; Intruderprufe LowE U Value=4.22; Intruderprufe SHGC Value=0.677; Intruderprufe U Value=5.72; Limit Sash Width Left Max=596 mm; Limit Sash Width Left Min=300 mm; Limit Window Width Max=2994 mm; Max Pane Area=0.39 m²; Outside Heavy Duty Interlocker=No; Sash Height=1107 mm  [stored 3.63189 ft]; Sash Width Left=448 mm; Sash Width Right=448 mm; Standard Interlocker=Yes; Width=890 mm  [stored 2.91995 ft]; Windload Design=1500 mm  [stored 4.92126 ft]
- Elite-0912OX-2000Pa: Area Left Sash Glazing=0.39 m²; Area Right Sash Glazing=0.39 m²; Clearvue SHGC Value=0.714; Clearvue U Value=5.86; Custom Windload=2000 mm  [stored 6.56168 ft]; Custom Window Height=1190 mm  [stored 3.9042 ft]; Custom Window Width=890 mm  [stored 2.91995 ft]; Energy Advantage SHGC Value=0.639; Energy Advantage U Value=4.4; Height=1190 mm  [stored 3.9042 ft]; Inside Heavy Duty Interlocker=No; Interlocker Configuration=0 mm  [stored 0 ft]; Intruderprufe LowE SHGC Value=0.594; Intruderprufe LowE U Value=4.22; Intruderprufe SHGC Value=0.677; Intruderprufe U Value=5.72; Limit Sash Width Left Max=596 mm; Limit Sash Width Left Min=300 mm; Limit Window Width Max=2994 mm; Max Pane Area=0.39 m²; Outside Heavy Duty Interlocker=No; Sash Height=1107 mm  [stored 3.63189 ft]; Sash Width Left=448 mm; Sash Width Right=448 mm; Standard Interlocker=Yes; Width=890 mm  [stored 2.91995 ft]; Windload Design=2000 mm  [stored 6.56168 ft]
- Elite-0915OX-1500Pa: Area Left Sash Glazing=0.51 m²; Area Right Sash Glazing=0.51 m²; Clearvue SHGC Value=0.724; Clearvue U Value=5.89; Custom Windload=1500 mm  [stored 4.92126 ft]; Custom Window Height=1490 mm  [stored 4.88845 ft]; Custom Window Width=890 mm  [stored 2.91995 ft]; Energy Advantage SHGC Value=0.649; Energy Advantage U Value=4.39; Height=1490 mm  [stored 4.88845 ft]; Inside Heavy Duty Interlocker=Yes; Interlocker Configuration=1 mm  [stored 0.00328084 ft]; Intruderprufe LowE SHGC Value=0.603; Intruderprufe LowE U Value=4.2; Intruderprufe SHGC Value=0.687; Intruderprufe U Value=5.75; Limit Sash Width Left Max=596 mm; Limit Sash Width Left Min=300 mm; Limit Window Width Max=2994 mm; Max Pane Area=0.51 m²; Outside Heavy Duty Interlocker=No; Sash Height=1407 mm  [stored 4.61614 ft]; Sash Width Left=448 mm; Sash Width Right=448 mm; Standard Interlocker=No; Width=890 mm  [stored 2.91995 ft]; Windload Design=1500 mm  [stored 4.92126 ft]
- Elite-0915OX-2000Pa: Area Left Sash Glazing=0.51 m²; Area Right Sash Glazing=0.51 m²; Clearvue SHGC Value=0.724; Clearvue U Value=5.89; Custom Windload=2000 mm  [stored 6.56168 ft]; Custom Window Height=1490 mm  [stored 4.88845 ft]; Custom Window Width=890 mm  [stored 2.91995 ft]; Energy Advantage SHGC Value=0.649; Energy Advantage U Value=4.39; Height=1490 mm  [stored 4.88845 ft]; Inside Heavy Duty Interlocker=Yes; Interlocker Configuration=1 mm  [stored 0.00328084 ft]; Intruderprufe LowE SHGC Value=0.603; Intruderprufe LowE U Value=4.2; Intruderprufe SHGC Value=0.687; Intruderprufe U Value=5.75; Limit Sash Width Left Max=596 mm; Limit Sash Width Left Min=300 mm; Limit Window Width Max=2994 mm; Max Pane Area=0.51 m²; Outside Heavy Duty Interlocker=No; Sash Height=1407 mm  [stored 4.61614 ft]; Sash Width Left=448 mm; Sash Width Right=448 mm; Standard Interlocker=No; Width=890 mm  [stored 2.91995 ft]; Windload Design=2000 mm  [stored 6.56168 ft]
- Elite-0918OX-1500Pa: Area Left Sash Glazing=0.62 m²; Area Right Sash Glazing=0.62 m²; Clearvue SHGC Value=0.733; Clearvue U Value=6.08; Custom Windload=1500 mm  [stored 4.92126 ft]; Custom Window Height=1790 mm  [stored 5.8727 ft]; Custom Window Width=890 mm  [stored 2.91995 ft]; Energy Advantage SHGC Value=0.657; Energy Advantage U Value=4.54; Height=1790 mm  [stored 5.8727 ft]; Inside Heavy Duty Interlocker=Yes; Interlocker Configuration=1 mm  [stored 0.00328084 ft]; Intruderprufe LowE SHGC Value=0.611; Intruderprufe LowE U Value=4.37; Intruderprufe SHGC Value=0.695; Intruderprufe U Value=5.59; Limit Sash Width Left Max=596 mm; Limit Sash Width Left Min=300 mm; Limit Window Width Max=1490 mm  [stored 4.88845 ft]; Max Pane Area=0.62 m²; Outside Heavy Duty Interlocker=No; Sash Height=1707 mm; Sash Width Left=448 mm; Sash Width Right=448 mm; Standard Interlocker=No; Width=890 mm  [stored 2.91995 ft]; Windload Design=1500 mm  [stored 4.92126 ft]
- Elite-0918OX-2000Pa: Area Left Sash Glazing=0.62 m²; Area Right Sash Glazing=0.62 m²; Clearvue SHGC Value=0.733; Clearvue U Value=6.08; Custom Windload=2000 mm  [stored 6.56168 ft]; Custom Window Height=1790 mm  [stored 5.8727 ft]; Custom Window Width=890 mm  [stored 2.91995 ft]; Energy Advantage SHGC Value=0.657; Energy Advantage U Value=4.54; Height=1790 mm  [stored 5.8727 ft]; Inside Heavy Duty Interlocker=Yes; Interlocker Configuration=2 mm  [stored 0.00656168 ft]; Intruderprufe LowE SHGC Value=0.611; Intruderprufe LowE U Value=4.37; Intruderprufe SHGC Value=0.695; Intruderprufe U Value=5.59; Limit Sash Width Left Max=596 mm; Limit Sash Width Left Min=300 mm; Limit Window Width Max=890 mm  [stored 2.91995 ft]; Max Pane Area=0.62 m²; Outside Heavy Duty Interlocker=Yes; Sash Height=1707 mm; Sash Width Left=448 mm; Sash Width Right=448 mm; Standard Interlocker=No; Width=890 mm  [stored 2.91995 ft]; Windload Design=2000 mm  [stored 6.56168 ft]
- Elite-1206OX-1500Pa: Area Left Sash Glazing=0.22 m²; Area Right Sash Glazing=0.22 m²; Clearvue SHGC Value=0.675; Clearvue U Value=5.69; Custom Windload=1500 mm  [stored 4.92126 ft]; Custom Window Height=590 mm  [stored 1.9357 ft]; Custom Window Width=1190 mm  [stored 3.9042 ft]; Energy Advantage SHGC Value=0.605; Energy Advantage U Value=4.38; Height=590 mm  [stored 1.9357 ft]; Inside Heavy Duty Interlocker=No; Interlocker Configuration=0 mm  [stored 0 ft]; Intruderprufe LowE SHGC Value=0.563; Intruderprufe LowE U Value=4.22; Intruderprufe SHGC Value=0.641; Intruderprufe U Value=5.57; Limit Sash Width Left Max=896 mm; Limit Sash Width Left Min=300 mm; Limit Window Width Max=2994 mm; Max Pane Area=0.22 m²; Outside Heavy Duty Interlocker=No; Sash Height=507 mm; Sash Width Left=598 mm; Sash Width Right=598 mm; Standard Interlocker=Yes; Width=1190 mm  [stored 3.9042 ft]; Windload Design=1500 mm  [stored 4.92126 ft]
- Elite-1206OX-2000Pa: Area Left Sash Glazing=0.22 m²; Area Right Sash Glazing=0.22 m²; Clearvue SHGC Value=0.675; Clearvue U Value=5.69; Custom Windload=2000 mm  [stored 6.56168 ft]; Custom Window Height=590 mm  [stored 1.9357 ft]; Custom Window Width=1190 mm  [stored 3.9042 ft]; Energy Advantage SHGC Value=0.605; Energy Advantage U Value=4.38; Height=590 mm  [stored 1.9357 ft]; Inside Heavy Duty Interlocker=No; Interlocker Configuration=0 mm  [stored 0 ft]; Intruderprufe LowE SHGC Value=0.563; Intruderprufe LowE U Value=4.22; Intruderprufe SHGC Value=0.641; Intruderprufe U Value=5.57; Limit Sash Width Left Max=896 mm; Limit Sash Width Left Min=300 mm; Limit Window Width Max=2994 mm; Max Pane Area=0.22 m²; Outside Heavy Duty Interlocker=No; Sash Height=507 mm; Sash Width Left=598 mm; Sash Width Right=598 mm; Standard Interlocker=Yes; Width=1190 mm  [stored 3.9042 ft]; Windload Design=2000 mm  [stored 6.56168 ft]
- Elite-1209OX-1500Pa: Area Left Sash Glazing=0.38 m²; Area Right Sash Glazing=0.38 m²; Clearvue SHGC Value=0.713; Clearvue U Value=5.79; Custom Windload=1500 mm  [stored 4.92126 ft]; Custom Window Height=890 mm  [stored 2.91995 ft]; Custom Window Width=1190 mm  [stored 3.9042 ft]; Energy Advantage SHGC Value=0.639; Energy Advantage U Value=4.31; Height=890 mm  [stored 2.91995 ft]; Inside Heavy Duty Interlocker=No; Interlocker Configuration=0 mm  [stored 0 ft]; Intruderprufe LowE SHGC Value=0.594; Intruderprufe LowE U Value=4.15; Intruderprufe SHGC Value=0.676; Intruderprufe U Value=5.66; Limit Sash Width Left Max=896 mm; Limit Sash Width Left Min=300 mm; Limit Window Width Max=2994 mm; Max Pane Area=0.38 m²; Outside Heavy Duty Interlocker=No; Sash Height=807 mm  [stored 2.64764 ft]; Sash Width Left=598 mm; Sash Width Right=598 mm; Standard Interlocker=Yes; Width=1190 mm  [stored 3.9042 ft]; Windload Design=1500 mm  [stored 4.92126 ft]
- Elite-1209OX-2000Pa: Area Left Sash Glazing=0.38 m²; Area Right Sash Glazing=0.38 m²; Clearvue SHGC Value=0.713; Clearvue U Value=5.79; Custom Windload=2000 mm  [stored 6.56168 ft]; Custom Window Height=890 mm  [stored 2.91995 ft]; Custom Window Width=1190 mm  [stored 3.9042 ft]; Energy Advantage SHGC Value=0.639; Energy Advantage U Value=4.31; Height=890 mm  [stored 2.91995 ft]; Inside Heavy Duty Interlocker=No; Interlocker Configuration=0 mm  [stored 0 ft]; Intruderprufe LowE SHGC Value=0.594; Intruderprufe LowE U Value=4.15; Intruderprufe SHGC Value=0.676; Intruderprufe U Value=5.66; Limit Sash Width Left Max=896 mm; Limit Sash Width Left Min=300 mm; Limit Window Width Max=2994 mm; Max Pane Area=0.38 m²; Outside Heavy Duty Interlocker=No; Sash Height=807 mm  [stored 2.64764 ft]; Sash Width Left=598 mm; Sash Width Right=598 mm; Standard Interlocker=Yes; Width=1190 mm  [stored 3.9042 ft]; Windload Design=2000 mm  [stored 6.56168 ft]
- Elite-1212OX-1500Pa: Area Left Sash Glazing=0.54 m²; Area Right Sash Glazing=0.54 m²; Clearvue SHGC Value=0.732; Clearvue U Value=5.84; Custom Windload=1500 mm  [stored 4.92126 ft]; Custom Window Height=1190 mm  [stored 3.9042 ft]; Custom Window Width=1190 mm  [stored 3.9042 ft]; Energy Advantage SHGC Value=0.655; Energy Advantage U Value=4.27; Height=1190 mm  [stored 3.9042 ft]; Inside Heavy Duty Interlocker=No; Interlocker Configuration=0 mm  [stored 0 ft]; Intruderprufe LowE SHGC Value=0.609; Intruderprufe LowE U Value=4.11; Intruderprufe SHGC Value=0.694; Intruderprufe U Value=5.7; Limit Sash Width Left Max=896 mm; Limit Sash Width Left Min=300 mm; Limit Window Width Max=2994 mm; Max Pane Area=0.54 m²; Outside Heavy Duty Interlocker=No; Sash Height=1107 mm  [stored 3.63189 ft]; Sash Width Left=598 mm; Sash Width Right=598 mm; Standard Interlocker=Yes; Width=1190 mm  [stored 3.9042 ft]; Windload Design=1500 mm  [stored 4.92126 ft]
- Elite-1212OX-2000Pa: Area Left Sash Glazing=0.54 m²; Area Right Sash Glazing=0.54 m²; Clearvue SHGC Value=0.732; Clearvue U Value=5.84; Custom Windload=2000 mm  [stored 6.56168 ft]; Custom Window Height=1190 mm  [stored 3.9042 ft]; Custom Window Width=1190 mm  [stored 3.9042 ft]; Energy Advantage SHGC Value=0.655; Energy Advantage U Value=4.27; Height=1190 mm  [stored 3.9042 ft]; Inside Heavy Duty Interlocker=Yes; Interlocker Configuration=1 mm  [stored 0.00328084 ft]; Intruderprufe LowE SHGC Value=0.609; Intruderprufe LowE U Value=4.11; Intruderprufe SHGC Value=0.694; Intruderprufe U Value=5.7; Limit Sash Width Left Max=896 mm; Limit Sash Width Left Min=300 mm; Limit Window Width Max=2994 mm; Max Pane Area=0.54 m²; Outside Heavy Duty Interlocker=No; Sash Height=1107 mm  [stored 3.63189 ft]; Sash Width Left=598 mm; Sash Width Right=598 mm; Standard Interlocker=No; Width=1190 mm  [stored 3.9042 ft]; Windload Design=2000 mm  [stored 6.56168 ft]
- Elite-1215OX-1500Pa: Area Left Sash Glazing=0.7 m²; Area Right Sash Glazing=0.7 m²; Clearvue SHGC Value=0.743; Clearvue U Value=5.87; Custom Windload=1500 mm  [stored 4.92126 ft]; Custom Window Height=1490 mm  [stored 4.88845 ft]; Custom Window Width=1190 mm  [stored 3.9042 ft]; Energy Advantage SHGC Value=0.665; Energy Advantage U Value=4.25; Height=1490 mm  [stored 4.88845 ft]; Inside Heavy Duty Interlocker=Yes; Interlocker Configuration=1 mm  [stored 0.00328084 ft]; Intruderprufe LowE SHGC Value=0.618; Intruderprufe LowE U Value=4.09; Intruderprufe SHGC Value=0.705; Intruderprufe U Value=5.73; Limit Sash Width Left Max=896 mm; Limit Sash Width Left Min=300 mm; Limit Window Width Max=2994 mm; Max Pane Area=0.7 m²; Outside Heavy Duty Interlocker=No; Sash Height=1407 mm  [stored 4.61614 ft]; Sash Width Left=598 mm; Sash Width Right=598 mm; Standard Interlocker=No; Width=1190 mm  [stored 3.9042 ft]; Windload Design=1500 mm  [stored 4.92126 ft]
- Elite-1215OX-2000Pa: Area Left Sash Glazing=0.7 m²; Area Right Sash Glazing=0.7 m²; Clearvue SHGC Value=0.743; Clearvue U Value=5.87; Custom Windload=2000 mm  [stored 6.56168 ft]; Custom Window Height=1490 mm  [stored 4.88845 ft]; Custom Window Width=1190 mm  [stored 3.9042 ft]; Energy Advantage SHGC Value=0.665; Energy Advantage U Value=4.25; Height=1490 mm  [stored 4.88845 ft]; Inside Heavy Duty Interlocker=Yes; Interlocker Configuration=1 mm  [stored 0.00328084 ft]; Intruderprufe LowE SHGC Value=0.618; Intruderprufe LowE U Value=4.09; Intruderprufe SHGC Value=0.705; Intruderprufe U Value=5.73; Limit Sash Width Left Max=896 mm; Limit Sash Width Left Min=300 mm; Limit Window Width Max=2994 mm; Max Pane Area=0.7 m²; Outside Heavy Duty Interlocker=No; Sash Height=1407 mm  [stored 4.61614 ft]; Sash Width Left=598 mm; Sash Width Right=598 mm; Standard Interlocker=No; Width=1190 mm  [stored 3.9042 ft]; Windload Design=2000 mm  [stored 6.56168 ft]
- Elite-1218OX-1500Pa: Area Left Sash Glazing=0.87 m²; Area Right Sash Glazing=0.87 m²; Clearvue SHGC Value=0.751; Clearvue U Value=5.88; Custom Windload=1500 mm  [stored 4.92126 ft]; Custom Window Height=1790 mm  [stored 5.8727 ft]; Custom Window Width=1190 mm  [stored 3.9042 ft]; Energy Advantage SHGC Value=0.672; Energy Advantage U Value=4.24; Height=1790 mm  [stored 5.8727 ft]; Inside Heavy Duty Interlocker=Yes; Interlocker Configuration=2 mm  [stored 0.00656168 ft]; Intruderprufe LowE SHGC Value=0.624; Intruderprufe LowE U Value=4.08; Intruderprufe SHGC Value=0.712; Intruderprufe U Value=5.75; Limit Sash Width Left Max=896 mm; Limit Sash Width Left Min=300 mm; Limit Window Width Max=1490 mm  [stored 4.88845 ft]; Max Pane Area=0.87 m²; Outside Heavy Duty Interlocker=Yes; Sash Height=1707 mm; Sash Width Left=598 mm; Sash Width Right=598 mm; Standard Interlocker=No; Width=1190 mm  [stored 3.9042 ft]; Windload Design=1500 mm  [stored 4.92126 ft]
- Elite-1506OX-1500Pa: Area Left Sash Glazing=0.28 m²; Area Right Sash Glazing=0.28 m²; Clearvue SHGC Value=0.684; Clearvue U Value=5.68; Custom Windload=1500 mm  [stored 4.92126 ft]; Custom Window Height=590 mm  [stored 1.9357 ft]; Custom Window Width=1490 mm  [stored 4.88845 ft]; Energy Advantage SHGC Value=0.613; Energy Advantage U Value=4.31; Height=590 mm  [stored 1.9357 ft]; Inside Heavy Duty Interlocker=No; Interlocker Configuration=0 mm  [stored 0 ft]; Intruderprufe LowE SHGC Value=0.57; Intruderprufe LowE U Value=4.17; Intruderprufe SHGC Value=0.649; Intruderprufe U Value=5.56; Limit Sash Width Left Max=1196 mm; Limit Sash Width Left Min=300 mm; Limit Window Width Max=2994 mm; Max Pane Area=0.28 m²; Outside Heavy Duty Interlocker=No; Sash Height=507 mm; Sash Width Left=748 mm; Sash Width Right=748 mm; Standard Interlocker=Yes; Width=1490 mm  [stored 4.88845 ft]; Windload Design=1500 mm  [stored 4.92126 ft]
- Elite-1506OX-2000Pa: Area Left Sash Glazing=0.28 m²; Area Right Sash Glazing=0.28 m²; Clearvue SHGC Value=0.684; Clearvue U Value=5.68; Custom Windload=2000 mm  [stored 6.56168 ft]; Custom Window Height=590 mm  [stored 1.9357 ft]; Custom Window Width=1490 mm  [stored 4.88845 ft]; Energy Advantage SHGC Value=0.613; Energy Advantage U Value=4.31; Height=590 mm  [stored 1.9357 ft]; Inside Heavy Duty Interlocker=No; Interlocker Configuration=0 mm  [stored 0 ft]; Intruderprufe LowE SHGC Value=0.57; Intruderprufe LowE U Value=4.17; Intruderprufe SHGC Value=0.649; Intruderprufe U Value=5.56; Limit Sash Width Left Max=1196 mm; Limit Sash Width Left Min=300 mm; Limit Window Width Max=2994 mm; Max Pane Area=0.28 m²; Outside Heavy Duty Interlocker=No; Sash Height=507 mm; Sash Width Left=748 mm; Sash Width Right=748 mm; Standard Interlocker=Yes; Width=1490 mm  [stored 4.88845 ft]; Windload Design=2000 mm  [stored 6.56168 ft]
- Elite-1509OX-1500Pa: Area Left Sash Glazing=0.49 m²; Area Right Sash Glazing=0.49 m²; Clearvue SHGC Value=0.723; Clearvue U Value=5.78; Custom Windload=1500 mm  [stored 4.92126 ft]; Custom Window Height=890 mm  [stored 2.91995 ft]; Custom Window Width=1490 mm  [stored 4.88845 ft]; Energy Advantage SHGC Value=0.648; Energy Advantage U Value=4.23; Height=890 mm  [stored 2.91995 ft]; Inside Heavy Duty Interlocker=No; Interlocker Configuration=0 mm  [stored 0 ft]; Intruderprufe LowE SHGC Value=0.602; Intruderprufe LowE U Value=4.09; Intruderprufe SHGC Value=0.686; Intruderprufe U Value=5.65; Limit Sash Width Left Max=1196 mm; Limit Sash Width Left Min=300 mm; Limit Window Width Max=2994 mm; Max Pane Area=0.49 m²; Outside Heavy Duty Interlocker=No; Sash Height=807 mm  [stored 2.64764 ft]; Sash Width Left=748 mm; Sash Width Right=748 mm; Standard Interlocker=Yes; Width=1490 mm  [stored 4.88845 ft]; Windload Design=1500 mm  [stored 4.92126 ft]
- Elite-1509OX-2000Pa: Area Left Sash Glazing=0.49 m²; Area Right Sash Glazing=0.49 m²; Clearvue SHGC Value=0.723; Clearvue U Value=5.78; Custom Windload=2000 mm  [stored 6.56168 ft]; Custom Window Height=890 mm  [stored 2.91995 ft]; Custom Window Width=1490 mm  [stored 4.88845 ft]; Energy Advantage SHGC Value=0.648; Energy Advantage U Value=4.23; Height=890 mm  [stored 2.91995 ft]; Inside Heavy Duty Interlocker=No; Interlocker Configuration=0 mm  [stored 0 ft]; Intruderprufe LowE SHGC Value=0.602; Intruderprufe LowE U Value=4.09; Intruderprufe SHGC Value=0.686; Intruderprufe U Value=5.65; Limit Sash Width Left Max=1196 mm; Limit Sash Width Left Min=300 mm; Limit Window Width Max=2994 mm; Max Pane Area=0.49 m²; Outside Heavy Duty Interlocker=No; Sash Height=807 mm  [stored 2.64764 ft]; Sash Width Left=748 mm; Sash Width Right=748 mm; Standard Interlocker=Yes; Width=1490 mm  [stored 4.88845 ft]; Windload Design=2000 mm  [stored 6.56168 ft]
- Elite-1512OX-1500Pa: Area Left Sash Glazing=0.7 m²; Area Right Sash Glazing=0.7 m²; Clearvue SHGC Value=0.743; Clearvue U Value=5.82; Custom Windload=1500 mm  [stored 4.92126 ft]; Custom Window Height=1190 mm  [stored 3.9042 ft]; Custom Window Width=1490 mm  [stored 4.88845 ft]; Energy Advantage SHGC Value=0.665; Energy Advantage U Value=4.19; Height=1190 mm  [stored 3.9042 ft]; Inside Heavy Duty Interlocker=Yes; Interlocker Configuration=1 mm  [stored 0.00328084 ft]; Intruderprufe LowE SHGC Value=0.618; Intruderprufe LowE U Value=4.05; Intruderprufe SHGC Value=0.704; Intruderprufe U Value=5.69; Limit Sash Width Left Max=1196 mm; Limit Sash Width Left Min=300 mm; Limit Window Width Max=2994 mm; Max Pane Area=0.7 m²; Outside Heavy Duty Interlocker=No; Sash Height=1107 mm  [stored 3.63189 ft]; Sash Width Left=748 mm; Sash Width Right=748 mm; Standard Interlocker=No; Width=1490 mm  [stored 4.88845 ft]; Windload Design=1500 mm  [stored 4.92126 ft]
- Elite-1512OX-2000Pa: Area Left Sash Glazing=0.7 m²; Area Right Sash Glazing=0.7 m²; Clearvue SHGC Value=0.743; Clearvue U Value=5.82; Custom Windload=2000 mm  [stored 6.56168 ft]; Custom Window Height=1190 mm  [stored 3.9042 ft]; Custom Window Width=1490 mm  [stored 4.88845 ft]; Energy Advantage SHGC Value=0.665; Energy Advantage U Value=4.19; Height=1190 mm  [stored 3.9042 ft]; Inside Heavy Duty Interlocker=Yes; Interlocker Configuration=1 mm  [stored 0.00328084 ft]; Intruderprufe LowE SHGC Value=0.618; Intruderprufe LowE U Value=4.05; Intruderprufe SHGC Value=0.704; Intruderprufe U Value=5.69; Limit Sash Width Left Max=1196 mm; Limit Sash Width Left Min=300 mm; Limit Window Width Max=2994 mm; Max Pane Area=0.7 m²; Outside Heavy Duty Interlocker=No; Sash Height=1107 mm  [stored 3.63189 ft]; Sash Width Left=748 mm; Sash Width Right=748 mm; Standard Interlocker=No; Width=1490 mm  [stored 4.88845 ft]; Windload Design=2000 mm  [stored 6.56168 ft]
- Elite-1515OX-1500Pa: Area Left Sash Glazing=0.9 m²; Area Right Sash Glazing=0.9 m²; Clearvue SHGC Value=0.755; Clearvue U Value=5.95; Custom Windload=1500 mm  [stored 4.92126 ft]; Custom Window Height=1490 mm  [stored 4.88845 ft]; Custom Window Width=1490 mm  [stored 4.88845 ft]; Energy Advantage SHGC Value=0.676; Energy Advantage U Value=4.27; Height=1490 mm  [stored 4.88845 ft]; Inside Heavy Duty Interlocker=Yes; Interlocker Configuration=1 mm  [stored 0.00328084 ft]; Intruderprufe LowE SHGC Value=0.628; Intruderprufe LowE U Value=4.13; Intruderprufe SHGC Value=0.7163; Intruderprufe U Value=5.82; Limit Sash Width Left Max=1196 mm; Limit Sash Width Left Min=300 mm; Limit Window Width Max=2994 mm; Max Pane Area=0.9 m²; Outside Heavy Duty Interlocker=No; Sash Height=1407 mm  [stored 4.61614 ft]; Sash Width Left=748 mm; Sash Width Right=748 mm; Standard Interlocker=No; Width=1490 mm  [stored 4.88845 ft]; Windload Design=1500 mm  [stored 4.92126 ft]
- Elite-1515OX-2000Pa: Area Left Sash Glazing=0.9 m²; Area Right Sash Glazing=0.9 m²; Clearvue SHGC Value=0.755; Clearvue U Value=5.95; Custom Windload=2000 mm  [stored 6.56168 ft]; Custom Window Height=1490 mm  [stored 4.88845 ft]; Custom Window Width=1490 mm  [stored 4.88845 ft]; Energy Advantage SHGC Value=0.676; Energy Advantage U Value=4.27; Height=1490 mm  [stored 4.88845 ft]; Inside Heavy Duty Interlocker=Yes; Interlocker Configuration=2 mm  [stored 0.00656168 ft]; Intruderprufe LowE SHGC Value=0.628; Intruderprufe LowE U Value=4.13; Intruderprufe SHGC Value=0.7163; Intruderprufe U Value=5.82; Limit Sash Width Left Max=1196 mm; Limit Sash Width Left Min=300 mm; Limit Window Width Max=2994 mm; Max Pane Area=0.9 m²; Outside Heavy Duty Interlocker=Yes; Sash Height=1407 mm  [stored 4.61614 ft]; Sash Width Left=748 mm; Sash Width Right=748 mm; Standard Interlocker=No; Width=1490 mm  [stored 4.88845 ft]; Windload Design=2000 mm  [stored 6.56168 ft]
- Elite-1518OX-1500Pa: Area Left Sash Glazing=1.11 m²; Area Right Sash Glazing=1.11 m²; Clearvue SHGC Value=0.762; Clearvue U Value=5.87; Custom Windload=1500 mm  [stored 4.92126 ft]; Custom Window Height=1790 mm  [stored 5.8727 ft]; Custom Window Width=1490 mm  [stored 4.88845 ft]; Energy Advantage SHGC Value=0.682; Energy Advantage U Value=4.15; Height=1790 mm  [stored 5.8727 ft]; Inside Heavy Duty Interlocker=Yes; Interlocker Configuration=2 mm  [stored 0.00656168 ft]; Intruderprufe LowE SHGC Value=0.634; Intruderprufe LowE U Value=4.01; Intruderprufe SHGC Value=0.723; Intruderprufe U Value=5.73; Limit Sash Width Left Max=1196 mm; Limit Sash Width Left Min=300 mm; Limit Window Width Max=1490 mm  [stored 4.88845 ft]; Max Pane Area=1.11 m²; Outside Heavy Duty Interlocker=Yes; Sash Height=1707 mm; Sash Width Left=748 mm; Sash Width Right=748 mm; Standard Interlocker=No; Width=1490 mm  [stored 4.88845 ft]; Windload Design=1500 mm  [stored 4.92126 ft]
- Elite-1806OX-1500Pa: Area Left Sash Glazing=0.35 m²; Area Right Sash Glazing=0.35 m²; Clearvue SHGC Value=0.691; Clearvue U Value=5.67; Custom Windload=1500 mm  [stored 4.92126 ft]; Custom Window Height=590 mm  [stored 1.9357 ft]; Custom Window Width=1790 mm  [stored 5.8727 ft]; Energy Advantage SHGC Value=0.618; Energy Advantage U Value=4.27; Height=590 mm  [stored 1.9357 ft]; Inside Heavy Duty Interlocker=No; Interlocker Configuration=0 mm  [stored 0 ft]; Intruderprufe LowE SHGC Value=0.575; Intruderprufe LowE U Value=4.14; Intruderprufe SHGC Value=0.655; Intruderprufe U Value=5.55; Limit Sash Width Left Max=1496 mm; Limit Sash Width Left Min=300 mm; Limit Window Width Max=2994 mm; Max Pane Area=0.35 m²; Outside Heavy Duty Interlocker=No; Sash Height=507 mm; Sash Width Left=898 mm; Sash Width Right=898 mm; Standard Interlocker=Yes; Width=1790 mm  [stored 5.8727 ft]; Windload Design=1500 mm  [stored 4.92126 ft]
- Elite-1806OX-2000Pa: Area Left Sash Glazing=0.35 m²; Area Right Sash Glazing=0.35 m²; Clearvue SHGC Value=0.691; Clearvue U Value=5.67; Custom Windload=2000 mm  [stored 6.56168 ft]; Custom Window Height=590 mm  [stored 1.9357 ft]; Custom Window Width=1790 mm  [stored 5.8727 ft]; Energy Advantage SHGC Value=0.618; Energy Advantage U Value=4.27; Height=590 mm  [stored 1.9357 ft]; Inside Heavy Duty Interlocker=No; Interlocker Configuration=0 mm  [stored 0 ft]; Intruderprufe LowE SHGC Value=0.575; Intruderprufe LowE U Value=4.14; Intruderprufe SHGC Value=0.655; Intruderprufe U Value=5.55; Limit Sash Width Left Max=1496 mm; Limit Sash Width Left Min=300 mm; Limit Window Width Max=2994 mm; Max Pane Area=0.35 m²; Outside Heavy Duty Interlocker=No; Sash Height=507 mm; Sash Width Left=898 mm; Sash Width Right=898 mm; Standard Interlocker=Yes; Width=1790 mm  [stored 5.8727 ft]; Windload Design=2000 mm  [stored 6.56168 ft]
- Elite-1809OX-1500Pa: Area Left Sash Glazing=0.6 m²; Area Right Sash Glazing=0.6 m²; Clearvue SHGC Value=0.73; Clearvue U Value=5.77; Custom Windload=1500 mm  [stored 4.92126 ft]; Custom Window Height=890 mm  [stored 2.91995 ft]; Custom Window Width=1790 mm  [stored 5.8727 ft]; Energy Advantage SHGC Value=0.654; Energy Advantage U Value=4.18; Height=890 mm  [stored 2.91995 ft]; Inside Heavy Duty Interlocker=No; Interlocker Configuration=0 mm  [stored 0 ft]; Intruderprufe LowE SHGC Value=0.608; Intruderprufe LowE U Value=4.05; Intruderprufe SHGC Value=0.696; Intruderprufe U Value=5.64; Limit Sash Width Left Max=1496 mm; Limit Sash Width Left Min=300 mm; Limit Window Width Max=2994 mm; Max Pane Area=0.6 m²; Outside Heavy Duty Interlocker=No; Sash Height=807 mm  [stored 2.64764 ft]; Sash Width Left=898 mm; Sash Width Right=898 mm; Standard Interlocker=Yes; Width=1790 mm  [stored 5.8727 ft]; Windload Design=1500 mm  [stored 4.92126 ft]
- Elite-1809OX-2000Pa: Area Left Sash Glazing=0.6 m²; Area Right Sash Glazing=0.6 m²; Clearvue SHGC Value=0.73; Clearvue U Value=5.77; Custom Windload=2000 mm  [stored 6.56168 ft]; Custom Window Height=890 mm  [stored 2.91995 ft]; Custom Window Width=1790 mm  [stored 5.8727 ft]; Energy Advantage SHGC Value=0.654; Energy Advantage U Value=4.18; Height=890 mm  [stored 2.91995 ft]; Inside Heavy Duty Interlocker=No; Interlocker Configuration=0 mm  [stored 0 ft]; Intruderprufe LowE SHGC Value=0.608; Intruderprufe LowE U Value=4.05; Intruderprufe SHGC Value=0.696; Intruderprufe U Value=5.64; Limit Sash Width Left Max=1496 mm; Limit Sash Width Left Min=300 mm; Limit Window Width Max=2994 mm; Max Pane Area=0.6 m²; Outside Heavy Duty Interlocker=No; Sash Height=807 mm  [stored 2.64764 ft]; Sash Width Left=898 mm; Sash Width Right=898 mm; Standard Interlocker=Yes; Width=1790 mm  [stored 5.8727 ft]; Windload Design=2000 mm  [stored 6.56168 ft]
- Elite-1812OX-1500Pa: Area Left Sash Glazing=0.85 m²; Area Right Sash Glazing=0.85 m²; Clearvue SHGC Value=0.75; Clearvue U Value=5.81; Custom Windload=1500 mm  [stored 4.92126 ft]; Custom Window Height=1190 mm  [stored 3.9042 ft]; Custom Window Width=1790 mm  [stored 5.8727 ft]; Energy Advantage SHGC Value=0.671; Energy Advantage U Value=4.14; Height=1190 mm  [stored 3.9042 ft]; Inside Heavy Duty Interlocker=Yes; Interlocker Configuration=1 mm  [stored 0.00328084 ft]; Intruderprufe LowE SHGC Value=0.624; Intruderprufe LowE U Value=4.01; Intruderprufe SHGC Value=0.711; Intruderprufe U Value=5.68; Limit Sash Width Left Max=1496 mm; Limit Sash Width Left Min=300 mm; Limit Window Width Max=2994 mm; Max Pane Area=0.85 m²; Outside Heavy Duty Interlocker=No; Sash Height=1107 mm  [stored 3.63189 ft]; Sash Width Left=898 mm; Sash Width Right=898 mm; Standard Interlocker=No; Width=1790 mm  [stored 5.8727 ft]; Windload Design=1500 mm  [stored 4.92126 ft]
- Elite-1812OX-2000Pa: Area Left Sash Glazing=0.85 m²; Area Right Sash Glazing=0.85 m²; Clearvue SHGC Value=0.75; Clearvue U Value=5.81; Custom Windload=2000 mm  [stored 6.56168 ft]; Custom Window Height=1190 mm  [stored 3.9042 ft]; Custom Window Width=1790 mm  [stored 5.8727 ft]; Energy Advantage SHGC Value=0.671; Energy Advantage U Value=4.14; Height=1190 mm  [stored 3.9042 ft]; Inside Heavy Duty Interlocker=Yes; Interlocker Configuration=1 mm  [stored 0.00328084 ft]; Intruderprufe LowE SHGC Value=0.624; Intruderprufe LowE U Value=4.01; Intruderprufe SHGC Value=0.711; Intruderprufe U Value=5.68; Limit Sash Width Left Max=1496 mm; Limit Sash Width Left Min=300 mm; Limit Window Width Max=2994 mm; Max Pane Area=0.85 m²; Outside Heavy Duty Interlocker=No; Sash Height=1107 mm  [stored 3.63189 ft]; Sash Width Left=898 mm; Sash Width Right=898 mm; Standard Interlocker=No; Width=1790 mm  [stored 5.8727 ft]; Windload Design=2000 mm  [stored 6.56168 ft]
- Elite-1815OX-1500Pa: Area Left Sash Glazing=1.1 m²; Area Right Sash Glazing=1.1 m²; Clearvue SHGC Value=0.762; Clearvue U Value=5.84; Custom Windload=1500 mm  [stored 4.92126 ft]; Custom Window Height=1490 mm  [stored 4.88845 ft]; Custom Window Width=1790 mm  [stored 5.8727 ft]; Energy Advantage SHGC Value=0.682; Energy Advantage U Value=4.11; Height=1490 mm  [stored 4.88845 ft]; Inside Heavy Duty Interlocker=Yes; Interlocker Configuration=1 mm  [stored 0.00328084 ft]; Intruderprufe LowE SHGC Value=0.633; Intruderprufe LowE U Value=3.98; Intruderprufe SHGC Value=0.722; Intruderprufe U Value=5.71; Limit Sash Width Left Max=1496 mm; Limit Sash Width Left Min=300 mm; Limit Window Width Max=2994 mm; Max Pane Area=1.1 m²; Outside Heavy Duty Interlocker=No; Sash Height=1407 mm  [stored 4.61614 ft]; Sash Width Left=898 mm; Sash Width Right=898 mm; Standard Interlocker=No; Width=1790 mm  [stored 5.8727 ft]; Windload Design=1500 mm  [stored 4.92126 ft]
- Elite-1815OX-2000Pa: Area Left Sash Glazing=1.1 m²; Area Right Sash Glazing=1.1 m²; Clearvue SHGC Value=0.762; Clearvue U Value=5.84; Custom Windload=2000 mm  [stored 6.56168 ft]; Custom Window Height=1490 mm  [stored 4.88845 ft]; Custom Window Width=1790 mm  [stored 5.8727 ft]; Energy Advantage SHGC Value=0.682; Energy Advantage U Value=4.11; Height=1490 mm  [stored 4.88845 ft]; Inside Heavy Duty Interlocker=Yes; Interlocker Configuration=2 mm  [stored 0.00656168 ft]; Intruderprufe LowE SHGC Value=0.633; Intruderprufe LowE U Value=3.98; Intruderprufe SHGC Value=0.722; Intruderprufe U Value=5.71; Limit Sash Width Left Max=1496 mm; Limit Sash Width Left Min=300 mm; Limit Window Width Max=2994 mm; Max Pane Area=1.1 m²; Outside Heavy Duty Interlocker=Yes; Sash Height=1407 mm  [stored 4.61614 ft]; Sash Width Left=898 mm; Sash Width Right=898 mm; Standard Interlocker=No; Width=1790 mm  [stored 5.8727 ft]; Windload Design=2000 mm  [stored 6.56168 ft]
- Elite-2106OX-1500Pa: Area Left Sash Glazing=0.41 m²; Area Right Sash Glazing=0.41 m²; Clearvue SHGC Value=0.695; Clearvue U Value=5.67; Custom Windload=1500 mm  [stored 4.92126 ft]; Custom Window Height=590 mm  [stored 1.9357 ft]; Custom Window Width=2090 mm  [stored 6.85696 ft]; Energy Advantage SHGC Value=0.622; Energy Advantage U Value=4.24; Height=590 mm  [stored 1.9357 ft]; Inside Heavy Duty Interlocker=No; Interlocker Configuration=0 mm  [stored 0 ft]; Intruderprufe LowE SHGC Value=0.579; Intruderprufe LowE U Value=4.12; Intruderprufe SHGC Value=0.659; Intruderprufe U Value=5.55; Limit Sash Width Left Max=1500 mm  [stored 4.92126 ft]; Limit Sash Width Left Min=596 mm; Limit Window Width Max=2994 mm; Max Pane Area=0.41 m²; Outside Heavy Duty Interlocker=No; Sash Height=507 mm; Sash Width Left=1048 mm; Sash Width Right=1048 mm; Standard Interlocker=Yes; Width=2090 mm  [stored 6.85696 ft]; Windload Design=1500 mm  [stored 4.92126 ft]
- Elite-2106OX-2000Pa: Area Left Sash Glazing=0.41 m²; Area Right Sash Glazing=0.41 m²; Clearvue SHGC Value=0.695; Clearvue U Value=5.67; Custom Windload=2000 mm  [stored 6.56168 ft]; Custom Window Height=590 mm  [stored 1.9357 ft]; Custom Window Width=2090 mm  [stored 6.85696 ft]; Energy Advantage SHGC Value=0.622; Energy Advantage U Value=4.24; Height=590 mm  [stored 1.9357 ft]; Inside Heavy Duty Interlocker=No; Interlocker Configuration=0 mm  [stored 0 ft]; Intruderprufe LowE SHGC Value=0.579; Intruderprufe LowE U Value=4.12; Intruderprufe SHGC Value=0.659; Intruderprufe U Value=5.55; Limit Sash Width Left Max=1500 mm  [stored 4.92126 ft]; Limit Sash Width Left Min=596 mm; Limit Window Width Max=2994 mm; Max Pane Area=0.41 m²; Outside Heavy Duty Interlocker=No; Sash Height=507 mm; Sash Width Left=1048 mm; Sash Width Right=1048 mm; Standard Interlocker=Yes; Width=2090 mm  [stored 6.85696 ft]; Windload Design=2000 mm  [stored 6.56168 ft]
- Elite-2109OX-1500Pa: Area Left Sash Glazing=0.7 m²; Area Right Sash Glazing=0.7 m²; Clearvue SHGC Value=0.735; Clearvue U Value=5.76; Custom Windload=1500 mm  [stored 4.92126 ft]; Custom Window Height=890 mm  [stored 2.91995 ft]; Custom Window Width=2090 mm  [stored 6.85696 ft]; Energy Advantage SHGC Value=0.658; Energy Advantage U Value=4.15; Height=890 mm  [stored 2.91995 ft]; Inside Heavy Duty Interlocker=No; Interlocker Configuration=0 mm  [stored 0 ft]; Intruderprufe LowE SHGC Value=0.612; Intruderprufe LowE U Value=4.03; Intruderprufe SHGC Value=0.697; Intruderprufe U Value=5.63; Limit Sash Width Left Max=1500 mm  [stored 4.92126 ft]; Limit Sash Width Left Min=596 mm; Limit Window Width Max=2994 mm; Max Pane Area=0.7 m²; Outside Heavy Duty Interlocker=No; Sash Height=807 mm  [stored 2.64764 ft]; Sash Width Left=1048 mm; Sash Width Right=1048 mm; Standard Interlocker=Yes; Width=2090 mm  [stored 6.85696 ft]; Windload Design=1500 mm  [stored 4.92126 ft]
- Elite-2109OX-2000Pa: Area Left Sash Glazing=0.7 m²; Area Right Sash Glazing=0.7 m²; Clearvue SHGC Value=0.735; Clearvue U Value=5.76; Custom Windload=2000 mm  [stored 6.56168 ft]; Custom Window Height=890 mm  [stored 2.91995 ft]; Custom Window Width=2090 mm  [stored 6.85696 ft]; Energy Advantage SHGC Value=0.658; Energy Advantage U Value=4.15; Height=890 mm  [stored 2.91995 ft]; Inside Heavy Duty Interlocker=No; Interlocker Configuration=0 mm  [stored 0 ft]; Intruderprufe LowE SHGC Value=0.612; Intruderprufe LowE U Value=4.03; Intruderprufe SHGC Value=0.697; Intruderprufe U Value=5.63; Limit Sash Width Left Max=1500 mm  [stored 4.92126 ft]; Limit Sash Width Left Min=596 mm; Limit Window Width Max=2994 mm; Max Pane Area=0.7 m²; Outside Heavy Duty Interlocker=No; Sash Height=807 mm  [stored 2.64764 ft]; Sash Width Left=1048 mm; Sash Width Right=1048 mm; Standard Interlocker=Yes; Width=2090 mm  [stored 6.85696 ft]; Windload Design=2000 mm  [stored 6.56168 ft]
- Elite-2112OX-1500Pa: Area Left Sash Glazing=1 m²; Area Right Sash Glazing=1 m²; Clearvue SHGC Value=0.755; Clearvue U Value=5.8; Custom Windload=1500 mm  [stored 4.92126 ft]; Custom Window Height=1190 mm  [stored 3.9042 ft]; Custom Window Width=2090 mm  [stored 6.85696 ft]; Energy Advantage SHGC Value=0.676; Energy Advantage U Value=4.1; Height=1190 mm  [stored 3.9042 ft]; Inside Heavy Duty Interlocker=Yes; Interlocker Configuration=1 mm  [stored 0.00328084 ft]; Intruderprufe LowE SHGC Value=0.628; Intruderprufe LowE U Value=3.98; Intruderprufe SHGC Value=0.716; Intruderprufe U Value=5.67; Limit Sash Width Left Max=1500 mm  [stored 4.92126 ft]; Limit Sash Width Left Min=596 mm; Limit Window Width Max=2994 mm; Max Pane Area=1 m²; Outside Heavy Duty Interlocker=No; Sash Height=1107 mm  [stored 3.63189 ft]; Sash Width Left=1048 mm; Sash Width Right=1048 mm; Standard Interlocker=No; Width=2090 mm  [stored 6.85696 ft]; Windload Design=1500 mm  [stored 4.92126 ft]
- Elite-2112OX-2000Pa: Area Left Sash Glazing=1 m²; Area Right Sash Glazing=1 m²; Clearvue SHGC Value=0.755; Clearvue U Value=5.8; Custom Windload=2000 mm  [stored 6.56168 ft]; Custom Window Height=1190 mm  [stored 3.9042 ft]; Custom Window Width=2090 mm  [stored 6.85696 ft]; Energy Advantage SHGC Value=0.676; Energy Advantage U Value=4.1; Height=1190 mm  [stored 3.9042 ft]; Inside Heavy Duty Interlocker=Yes; Interlocker Configuration=1 mm  [stored 0.00328084 ft]; Intruderprufe LowE SHGC Value=0.628; Intruderprufe LowE U Value=3.98; Intruderprufe SHGC Value=0.716; Intruderprufe U Value=5.67; Limit Sash Width Left Max=1500 mm  [stored 4.92126 ft]; Limit Sash Width Left Min=596 mm; Limit Window Width Max=2994 mm; Max Pane Area=1 m²; Outside Heavy Duty Interlocker=No; Sash Height=1107 mm  [stored 3.63189 ft]; Sash Width Left=1048 mm; Sash Width Right=1048 mm; Standard Interlocker=No; Width=2090 mm  [stored 6.85696 ft]; Windload Design=2000 mm  [stored 6.56168 ft]
- Elite-2115OX-1500Pa: Area Left Sash Glazing=1.3 m²; Area Right Sash Glazing=1.3 m²; Clearvue SHGC Value=0.767; Clearvue U Value=5.83; Custom Windload=1500 mm  [stored 4.92126 ft]; Custom Window Height=1490 mm  [stored 4.88845 ft]; Custom Window Width=2090 mm  [stored 6.85696 ft]; Energy Advantage SHGC Value=0.686; Energy Advantage U Value=4.07; Height=1490 mm  [stored 4.88845 ft]; Inside Heavy Duty Interlocker=Yes; Interlocker Configuration=2 mm  [stored 0.00656168 ft]; Intruderprufe LowE SHGC Value=0.638; Intruderprufe LowE U Value=3.95; Intruderprufe SHGC Value=0.727; Intruderprufe U Value=5.7; Limit Sash Width Left Max=1500 mm  [stored 4.92126 ft]; Limit Sash Width Left Min=596 mm; Limit Window Width Max=2994 mm; Max Pane Area=1.3 m²; Outside Heavy Duty Interlocker=Yes; Sash Height=1407 mm  [stored 4.61614 ft]; Sash Width Left=1048 mm; Sash Width Right=1048 mm; Standard Interlocker=No; Width=2090 mm  [stored 6.85696 ft]; Windload Design=1500 mm  [stored 4.92126 ft]
- Elite-2115OX-2000Pa: Area Left Sash Glazing=1.3 m²; Area Right Sash Glazing=1.3 m²; Clearvue SHGC Value=0.767; Clearvue U Value=5.83; Custom Windload=2000 mm  [stored 6.56168 ft]; Custom Window Height=1490 mm  [stored 4.88845 ft]; Custom Window Width=2090 mm  [stored 6.85696 ft]; Energy Advantage SHGC Value=0.686; Energy Advantage U Value=4.07; Height=1490 mm  [stored 4.88845 ft]; Inside Heavy Duty Interlocker=Yes; Interlocker Configuration=2 mm  [stored 0.00656168 ft]; Intruderprufe LowE SHGC Value=0.638; Intruderprufe LowE U Value=3.95; Intruderprufe SHGC Value=0.727; Intruderprufe U Value=5.7; Limit Sash Width Left Max=1500 mm  [stored 4.92126 ft]; Limit Sash Width Left Min=596 mm; Limit Window Width Max=2994 mm; Max Pane Area=1.3 m²; Outside Heavy Duty Interlocker=Yes; Sash Height=1407 mm  [stored 4.61614 ft]; Sash Width Left=1048 mm; Sash Width Right=1048 mm; Standard Interlocker=No; Width=2090 mm  [stored 6.85696 ft]; Windload Design=2000 mm  [stored 6.56168 ft]
- Elite-2406OX-1500Pa: Area Left Sash Glazing=0.47 m²; Area Right Sash Glazing=0.47 m²; Clearvue SHGC Value=0.698; Clearvue U Value=5.66; Custom Windload=1500 mm  [stored 4.92126 ft]; Custom Window Height=590 mm  [stored 1.9357 ft]; Custom Window Width=2390 mm  [stored 7.84121 ft]; Energy Advantage SHGC Value=0.625; Energy Advantage U Value=4.22; Height=590 mm  [stored 1.9357 ft]; Inside Heavy Duty Interlocker=No; Interlocker Configuration=0 mm  [stored 0 ft]; Intruderprufe LowE SHGC Value=0.582; Intruderprufe LowE U Value=4.1; Intruderprufe SHGC Value=0.662; Intruderprufe U Value=5.55; Limit Sash Width Left Max=1500 mm  [stored 4.92126 ft]; Limit Sash Width Left Min=896 mm; Limit Window Width Max=2994 mm; Max Pane Area=0.47 m²; Outside Heavy Duty Interlocker=No; Sash Height=507 mm; Sash Width Left=1198 mm; Sash Width Right=1198 mm; Standard Interlocker=Yes; Width=2390 mm  [stored 7.84121 ft]; Windload Design=1500 mm  [stored 4.92126 ft]
- Elite-2406OX-2000Pa: Area Left Sash Glazing=0.47 m²; Area Right Sash Glazing=0.47 m²; Clearvue SHGC Value=0.698; Clearvue U Value=5.66; Custom Windload=2000 mm  [stored 6.56168 ft]; Custom Window Height=590 mm  [stored 1.9357 ft]; Custom Window Width=2390 mm  [stored 7.84121 ft]; Energy Advantage SHGC Value=0.625; Energy Advantage U Value=4.22; Height=590 mm  [stored 1.9357 ft]; Inside Heavy Duty Interlocker=No; Interlocker Configuration=0 mm  [stored 0 ft]; Intruderprufe LowE SHGC Value=0.582; Intruderprufe LowE U Value=4.1; Intruderprufe SHGC Value=0.662; Intruderprufe U Value=5.55; Limit Sash Width Left Max=1500 mm  [stored 4.92126 ft]; Limit Sash Width Left Min=896 mm; Limit Window Width Max=2994 mm; Max Pane Area=0.47 m²; Outside Heavy Duty Interlocker=No; Sash Height=507 mm; Sash Width Left=1198 mm; Sash Width Right=1198 mm; Standard Interlocker=Yes; Width=2390 mm  [stored 7.84121 ft]; Windload Design=2000 mm  [stored 6.56168 ft]
- Elite-2409OX-1500Pa: Area Left Sash Glazing=0.81 m²; Area Right Sash Glazing=0.81 m²; Clearvue SHGC Value=0.739; Clearvue U Value=5.75; Custom Windload=1500 mm  [stored 4.92126 ft]; Custom Window Height=890 mm  [stored 2.91995 ft]; Custom Window Width=2390 mm  [stored 7.84121 ft]; Energy Advantage SHGC Value=0.661; Energy Advantage U Value=4.12; Height=890 mm  [stored 2.91995 ft]; Inside Heavy Duty Interlocker=No; Interlocker Configuration=0 mm  [stored 0 ft]; Intruderprufe LowE SHGC Value=0.615; Intruderprufe LowE U Value=4; Intruderprufe SHGC Value=0.701; Intruderprufe U Value=5.63; Limit Sash Width Left Max=1500 mm  [stored 4.92126 ft]; Limit Sash Width Left Min=896 mm; Limit Window Width Max=2994 mm; Max Pane Area=0.81 m²; Outside Heavy Duty Interlocker=No; Sash Height=807 mm  [stored 2.64764 ft]; Sash Width Left=1198 mm; Sash Width Right=1198 mm; Standard Interlocker=Yes; Width=2390 mm  [stored 7.84121 ft]; Windload Design=1500 mm  [stored 4.92126 ft]
- Elite-2409OX-2000Pa: Area Left Sash Glazing=0.81 m²; Area Right Sash Glazing=0.81 m²; Clearvue SHGC Value=0.739; Clearvue U Value=5.75; Custom Windload=2000 mm  [stored 6.56168 ft]; Custom Window Height=890 mm  [stored 2.91995 ft]; Custom Window Width=2390 mm  [stored 7.84121 ft]; Energy Advantage SHGC Value=0.661; Energy Advantage U Value=4.12; Height=890 mm  [stored 2.91995 ft]; Inside Heavy Duty Interlocker=No; Interlocker Configuration=0 mm  [stored 0 ft]; Intruderprufe LowE SHGC Value=0.615; Intruderprufe LowE U Value=4; Intruderprufe SHGC Value=0.701; Intruderprufe U Value=5.63; Limit Sash Width Left Max=1500 mm  [stored 4.92126 ft]; Limit Sash Width Left Min=896 mm; Limit Window Width Max=2994 mm; Max Pane Area=0.81 m²; Outside Heavy Duty Interlocker=No; Sash Height=807 mm  [stored 2.64764 ft]; Sash Width Left=1198 mm; Sash Width Right=1198 mm; Standard Interlocker=Yes; Width=2390 mm  [stored 7.84121 ft]; Windload Design=2000 mm  [stored 6.56168 ft]
- Elite-2412OX-1500Pa: Area Left Sash Glazing=1.15 m²; Area Right Sash Glazing=1.15 m²; Clearvue SHGC Value=0.759; Clearvue U Value=5.8; Custom Windload=1500 mm  [stored 4.92126 ft]; Custom Window Height=1190 mm  [stored 3.9042 ft]; Custom Window Width=2390 mm  [stored 7.84121 ft]; Energy Advantage SHGC Value=0.679; Energy Advantage U Value=4.07; Height=1190 mm  [stored 3.9042 ft]; Inside Heavy Duty Interlocker=Yes; Interlocker Configuration=1 mm  [stored 0.00328084 ft]; Intruderprufe LowE SHGC Value=0.631; Intruderprufe LowE U Value=3.96; Intruderprufe SHGC Value=0.72; Intruderprufe U Value=5.67; Limit Sash Width Left Max=1500 mm  [stored 4.92126 ft]; Limit Sash Width Left Min=896 mm; Limit Window Width Max=2994 mm; Max Pane Area=1.15 m²; Outside Heavy Duty Interlocker=No; Sash Height=1107 mm  [stored 3.63189 ft]; Sash Width Left=1198 mm; Sash Width Right=1198 mm; Standard Interlocker=No; Width=2390 mm  [stored 7.84121 ft]; Windload Design=1500 mm  [stored 4.92126 ft]
- Elite-2412OX-2000Pa: Area Left Sash Glazing=1.15 m²; Area Right Sash Glazing=1.15 m²; Clearvue SHGC Value=0.759; Clearvue U Value=5.8; Custom Windload=2000 mm  [stored 6.56168 ft]; Custom Window Height=1190 mm  [stored 3.9042 ft]; Custom Window Width=2390 mm  [stored 7.84121 ft]; Energy Advantage SHGC Value=0.679; Energy Advantage U Value=4.07; Height=1190 mm  [stored 3.9042 ft]; Inside Heavy Duty Interlocker=Yes; Interlocker Configuration=1 mm  [stored 0.00328084 ft]; Intruderprufe LowE SHGC Value=0.631; Intruderprufe LowE U Value=3.96; Intruderprufe SHGC Value=0.72; Intruderprufe U Value=5.67; Limit Sash Width Left Max=1500 mm  [stored 4.92126 ft]; Limit Sash Width Left Min=896 mm; Limit Window Width Max=2994 mm; Max Pane Area=1.15 m²; Outside Heavy Duty Interlocker=No; Sash Height=1107 mm  [stored 3.63189 ft]; Sash Width Left=1198 mm; Sash Width Right=1198 mm; Standard Interlocker=No; Width=2390 mm  [stored 7.84121 ft]; Windload Design=2000 mm  [stored 6.56168 ft]
- Elite-2415OX-1500Pa: Area Left Sash Glazing=1.49 m²; Area Right Sash Glazing=1.49 m²; Clearvue SHGC Value=0.771; Clearvue U Value=5.82; Custom Windload=1500 mm  [stored 4.92126 ft]; Custom Window Height=1490 mm  [stored 4.88845 ft]; Custom Window Width=2390 mm  [stored 7.84121 ft]; Energy Advantage SHGC Value=0.69; Energy Advantage U Value=4.05; Height=1490 mm  [stored 4.88845 ft]; Inside Heavy Duty Interlocker=Yes; Interlocker Configuration=2 mm  [stored 0.00656168 ft]; Intruderprufe LowE SHGC Value=0.641; Intruderprufe LowE U Value=3.93; Intruderprufe SHGC Value=0.731; Intruderprufe U Value=5.69; Limit Sash Width Left Max=1500 mm  [stored 4.92126 ft]; Limit Sash Width Left Min=896 mm; Limit Window Width Max=2994 mm; Max Pane Area=1.49 m²; Outside Heavy Duty Interlocker=Yes; Sash Height=1407 mm  [stored 4.61614 ft]; Sash Width Left=1198 mm; Sash Width Right=1198 mm; Standard Interlocker=No; Width=2390 mm  [stored 7.84121 ft]; Windload Design=1500 mm  [stored 4.92126 ft]
- Elite-2415OX-2000Pa: Area Left Sash Glazing=1.49 m²; Area Right Sash Glazing=1.49 m²; Clearvue SHGC Value=0.771; Clearvue U Value=5.82; Custom Windload=2000 mm  [stored 6.56168 ft]; Custom Window Height=1490 mm  [stored 4.88845 ft]; Custom Window Width=2390 mm  [stored 7.84121 ft]; Energy Advantage SHGC Value=0.69; Energy Advantage U Value=4.05; Height=1490 mm  [stored 4.88845 ft]; Inside Heavy Duty Interlocker=Yes; Interlocker Configuration=2 mm  [stored 0.00656168 ft]; Intruderprufe LowE SHGC Value=0.641; Intruderprufe LowE U Value=3.93; Intruderprufe SHGC Value=0.731; Intruderprufe U Value=5.69; Limit Sash Width Left Max=1500 mm  [stored 4.92126 ft]; Limit Sash Width Left Min=896 mm; Limit Window Width Max=2994 mm; Max Pane Area=1.49 m²; Outside Heavy Duty Interlocker=Yes; Sash Height=1407 mm  [stored 4.61614 ft]; Sash Width Left=1198 mm; Sash Width Right=1198 mm; Standard Interlocker=No; Width=2390 mm  [stored 7.84121 ft]; Windload Design=2000 mm  [stored 6.56168 ft]
- Elite-2706OX-1500Pa: Area Left Sash Glazing=0.53 m²; Area Right Sash Glazing=0.53 m²; Clearvue SHGC Value=0.701; Clearvue U Value=5.66; Custom Windload=1500 mm  [stored 4.92126 ft]; Custom Window Height=590 mm  [stored 1.9357 ft]; Custom Window Width=2690 mm  [stored 8.82546 ft]; Energy Advantage SHGC Value=0.627; Energy Advantage U Value=4.2; Height=590 mm  [stored 1.9357 ft]; Inside Heavy Duty Interlocker=No; Interlocker Configuration=0 mm  [stored 0 ft]; Intruderprufe LowE SHGC Value=0.584; Intruderprufe LowE U Value=4.09; Intruderprufe SHGC Value=0.665; Intruderprufe U Value=5.54; Limit Sash Width Left Max=1500 mm  [stored 4.92126 ft]; Limit Sash Width Left Min=1196 mm; Limit Window Width Max=2994 mm; Max Pane Area=0.53 m²; Outside Heavy Duty Interlocker=No; Sash Height=507 mm; Sash Width Left=1348 mm; Sash Width Right=1348 mm; Standard Interlocker=Yes; Width=2690 mm  [stored 8.82546 ft]; Windload Design=1500 mm  [stored 4.92126 ft]
- Elite-2706OX-2000Pa: Area Left Sash Glazing=0.53 m²; Area Right Sash Glazing=0.53 m²; Clearvue SHGC Value=0.701; Clearvue U Value=5.66; Custom Windload=2000 mm  [stored 6.56168 ft]; Custom Window Height=590 mm  [stored 1.9357 ft]; Custom Window Width=2690 mm  [stored 8.82546 ft]; Energy Advantage SHGC Value=0.627; Energy Advantage U Value=4.2; Height=590 mm  [stored 1.9357 ft]; Inside Heavy Duty Interlocker=No; Interlocker Configuration=0 mm  [stored 0 ft]; Intruderprufe LowE SHGC Value=0.584; Intruderprufe LowE U Value=4.09; Intruderprufe SHGC Value=0.665; Intruderprufe U Value=5.54; Limit Sash Width Left Max=1500 mm  [stored 4.92126 ft]; Limit Sash Width Left Min=1196 mm; Limit Window Width Max=2994 mm; Max Pane Area=0.53 m²; Outside Heavy Duty Interlocker=No; Sash Height=507 mm; Sash Width Left=1348 mm; Sash Width Right=1348 mm; Standard Interlocker=Yes; Width=2690 mm  [stored 8.82546 ft]; Windload Design=2000 mm  [stored 6.56168 ft]
- Elite-2709OX-1500Pa: Area Left Sash Glazing=0.92 m²; Area Right Sash Glazing=0.92 m²; Clearvue SHGC Value=0.742; Clearvue U Value=5.75; Custom Windload=1500 mm  [stored 4.92126 ft]; Custom Window Height=890 mm  [stored 2.91995 ft]; Custom Window Width=2690 mm  [stored 8.82546 ft]; Energy Advantage SHGC Value=0.664; Energy Advantage U Value=4.1; Height=890 mm  [stored 2.91995 ft]; Inside Heavy Duty Interlocker=No; Interlocker Configuration=0 mm  [stored 0 ft]; Intruderprufe LowE SHGC Value=0.617; Intruderprufe LowE U Value=3.99; Intruderprufe SHGC Value=0.704; Intruderprufe U Value=5.62; Limit Sash Width Left Max=1500 mm  [stored 4.92126 ft]; Limit Sash Width Left Min=1196 mm; Limit Window Width Max=2994 mm; Max Pane Area=0.92 m²; Outside Heavy Duty Interlocker=No; Sash Height=807 mm  [stored 2.64764 ft]; Sash Width Left=1348 mm; Sash Width Right=1348 mm; Standard Interlocker=Yes; Width=2690 mm  [stored 8.82546 ft]; Windload Design=1500 mm  [stored 4.92126 ft]
- Elite-2709OX-2000Pa: Area Left Sash Glazing=0.92 m²; Area Right Sash Glazing=0.92 m²; Clearvue SHGC Value=0.742; Clearvue U Value=5.75; Custom Windload=2000 mm  [stored 6.56168 ft]; Custom Window Height=890 mm  [stored 2.91995 ft]; Custom Window Width=2690 mm  [stored 8.82546 ft]; Energy Advantage SHGC Value=0.664; Energy Advantage U Value=4.1; Height=890 mm  [stored 2.91995 ft]; Inside Heavy Duty Interlocker=No; Interlocker Configuration=0 mm  [stored 0 ft]; Intruderprufe LowE SHGC Value=0.617; Intruderprufe LowE U Value=3.99; Intruderprufe SHGC Value=0.704; Intruderprufe U Value=5.62; Limit Sash Width Left Max=1500 mm  [stored 4.92126 ft]; Limit Sash Width Left Min=1196 mm; Limit Window Width Max=2994 mm; Max Pane Area=0.92 m²; Outside Heavy Duty Interlocker=No; Sash Height=807 mm  [stored 2.64764 ft]; Sash Width Left=1348 mm; Sash Width Right=1348 mm; Standard Interlocker=Yes; Width=2690 mm  [stored 8.82546 ft]; Windload Design=2000 mm  [stored 6.56168 ft]
- Elite-2712OX-1500Pa: Area Left Sash Glazing=1.31 m²; Area Right Sash Glazing=1.31 m²; Clearvue SHGC Value=0.762; Clearvue U Value=5.79; Custom Windload=1500 mm  [stored 4.92126 ft]; Custom Window Height=1190 mm  [stored 3.9042 ft]; Custom Window Width=2690 mm  [stored 8.82546 ft]; Energy Advantage SHGC Value=0.682; Energy Advantage U Value=4.05; Height=1190 mm  [stored 3.9042 ft]; Inside Heavy Duty Interlocker=Yes; Interlocker Configuration=1 mm  [stored 0.00328084 ft]; Intruderprufe LowE SHGC Value=0.634; Intruderprufe LowE U Value=3.94; Intruderprufe SHGC Value=0.723; Intruderprufe U Value=5.67; Limit Sash Width Left Max=1500 mm  [stored 4.92126 ft]; Limit Sash Width Left Min=1196 mm; Limit Window Width Max=2994 mm; Max Pane Area=1.31 m²; Outside Heavy Duty Interlocker=No; Sash Height=1107 mm  [stored 3.63189 ft]; Sash Width Left=1348 mm; Sash Width Right=1348 mm; Standard Interlocker=No; Width=2690 mm  [stored 8.82546 ft]; Windload Design=1500 mm  [stored 4.92126 ft]
- Elite-2712OX-2000Pa: Area Left Sash Glazing=1.31 m²; Area Right Sash Glazing=1.31 m²; Clearvue SHGC Value=0.762; Clearvue U Value=5.79; Custom Windload=2000 mm  [stored 6.56168 ft]; Custom Window Height=1190 mm  [stored 3.9042 ft]; Custom Window Width=2690 mm  [stored 8.82546 ft]; Energy Advantage SHGC Value=0.682; Energy Advantage U Value=4.05; Height=1190 mm  [stored 3.9042 ft]; Inside Heavy Duty Interlocker=Yes; Interlocker Configuration=1 mm  [stored 0.00328084 ft]; Intruderprufe LowE SHGC Value=0.634; Intruderprufe LowE U Value=3.94; Intruderprufe SHGC Value=0.723; Intruderprufe U Value=5.67; Limit Sash Width Left Max=1500 mm  [stored 4.92126 ft]; Limit Sash Width Left Min=1196 mm; Limit Window Width Max=2994 mm; Max Pane Area=1.31 m²; Outside Heavy Duty Interlocker=No; Sash Height=1107 mm  [stored 3.63189 ft]; Sash Width Left=1348 mm; Sash Width Right=1348 mm; Standard Interlocker=No; Width=2690 mm  [stored 8.82546 ft]; Windload Design=2000 mm  [stored 6.56168 ft]
- Elite-2715OX-1500Pa: Area Left Sash Glazing=1.69 m²; Area Right Sash Glazing=1.69 m²; Clearvue SHGC Value=0.774; Clearvue U Value=5.82; Custom Windload=1500 mm  [stored 4.92126 ft]; Custom Window Height=1490 mm  [stored 4.88845 ft]; Custom Window Width=2690 mm  [stored 8.82546 ft]; Energy Advantage SHGC Value=0.692; Energy Advantage U Value=4.02; Height=1490 mm  [stored 4.88845 ft]; Inside Heavy Duty Interlocker=Yes; Interlocker Configuration=2 mm  [stored 0.00656168 ft]; Intruderprufe LowE SHGC Value=0.643; Intruderprufe LowE U Value=3.91; Intruderprufe SHGC Value=0.734; Intruderprufe U Value=5.69; Limit Sash Width Left Max=1500 mm  [stored 4.92126 ft]; Limit Sash Width Left Min=1196 mm; Limit Window Width Max=2994 mm; Max Pane Area=1.69 m²; Outside Heavy Duty Interlocker=Yes; Sash Height=1407 mm  [stored 4.61614 ft]; Sash Width Left=1348 mm; Sash Width Right=1348 mm; Standard Interlocker=No; Width=2690 mm  [stored 8.82546 ft]; Windload Design=1500 mm  [stored 4.92126 ft]
- Elite-2715OX-2000Pa: Area Left Sash Glazing=1.69 m²; Area Right Sash Glazing=1.69 m²; Clearvue SHGC Value=0.774; Clearvue U Value=5.82; Custom Windload=2000 mm  [stored 6.56168 ft]; Custom Window Height=1490 mm  [stored 4.88845 ft]; Custom Window Width=2690 mm  [stored 8.82546 ft]; Energy Advantage SHGC Value=0.692; Energy Advantage U Value=4.02; Height=1490 mm  [stored 4.88845 ft]; Inside Heavy Duty Interlocker=Yes; Interlocker Configuration=2 mm  [stored 0.00656168 ft]; Intruderprufe LowE SHGC Value=0.643; Intruderprufe LowE U Value=3.91; Intruderprufe SHGC Value=0.734; Intruderprufe U Value=5.69; Limit Sash Width Left Max=1500 mm  [stored 4.92126 ft]; Limit Sash Width Left Min=1196 mm; Limit Window Width Max=2994 mm; Max Pane Area=1.69 m²; Outside Heavy Duty Interlocker=Yes; Sash Height=1407 mm  [stored 4.61614 ft]; Sash Width Left=1348 mm; Sash Width Right=1348 mm; Standard Interlocker=No; Width=2690 mm  [stored 8.82546 ft]; Windload Design=2000 mm  [stored 6.56168 ft]
- Elite-3006OX-1500Pa: Area Left Sash Glazing=0.6 m²; Area Right Sash Glazing=0.6 m²; Clearvue SHGC Value=0.703; Clearvue U Value=5.66; Custom Windload=1500 mm  [stored 4.92126 ft]; Custom Window Height=590 mm  [stored 1.9357 ft]; Custom Window Width=2990 mm; Energy Advantage SHGC Value=0.629; Energy Advantage U Value=4.18; Height=590 mm  [stored 1.9357 ft]; Inside Heavy Duty Interlocker=No; Interlocker Configuration=0 mm  [stored 0 ft]; Intruderprufe LowE SHGC Value=0.585; Intruderprufe LowE U Value=4.08; Intruderprufe SHGC Value=0.667; Intruderprufe U Value=5.54; Limit Sash Width Left Max=1500 mm  [stored 4.92126 ft]; Limit Sash Width Left Min=1496 mm; Limit Window Width Max=2994 mm; Max Pane Area=0.6 m²; Outside Heavy Duty Interlocker=No; Sash Height=507 mm; Sash Width Left=1498 mm; Sash Width Right=1498 mm; Standard Interlocker=Yes; Width=2990 mm; Windload Design=1500 mm  [stored 4.92126 ft]
- Elite-3006OX-2000Pa: Area Left Sash Glazing=0.6 m²; Area Right Sash Glazing=0.6 m²; Clearvue SHGC Value=0.703; Clearvue U Value=5.66; Custom Windload=2000 mm  [stored 6.56168 ft]; Custom Window Height=590 mm  [stored 1.9357 ft]; Custom Window Width=2990 mm; Energy Advantage SHGC Value=0.629; Energy Advantage U Value=4.18; Height=590 mm  [stored 1.9357 ft]; Inside Heavy Duty Interlocker=No; Interlocker Configuration=0 mm  [stored 0 ft]; Intruderprufe LowE SHGC Value=0.585; Intruderprufe LowE U Value=4.08; Intruderprufe SHGC Value=0.667; Intruderprufe U Value=5.54; Limit Sash Width Left Max=1500 mm  [stored 4.92126 ft]; Limit Sash Width Left Min=1496 mm; Limit Window Width Max=2994 mm; Max Pane Area=0.6 m²; Outside Heavy Duty Interlocker=No; Sash Height=507 mm; Sash Width Left=1498 mm; Sash Width Right=1498 mm; Standard Interlocker=Yes; Width=2990 mm; Windload Design=2000 mm  [stored 6.56168 ft]
- Elite-3009OX-1500Pa: Area Left Sash Glazing=1.03 m²; Area Right Sash Glazing=1.03 m²; Clearvue SHGC Value=0.744; Clearvue U Value=5.75; Custom Windload=1500 mm  [stored 4.92126 ft]; Custom Window Height=890 mm  [stored 2.91995 ft]; Custom Window Width=2990 mm; Energy Advantage SHGC Value=0.66; Energy Advantage U Value=4.08; Height=890 mm  [stored 2.91995 ft]; Inside Heavy Duty Interlocker=No; Interlocker Configuration=0 mm  [stored 0 ft]; Intruderprufe LowE SHGC Value=0.619; Intruderprufe LowE U Value=3.98; Intruderprufe SHGC Value=0.706; Intruderprufe U Value=5.62; Limit Sash Width Left Max=1500 mm  [stored 4.92126 ft]; Limit Sash Width Left Min=1496 mm; Limit Window Width Max=2994 mm; Max Pane Area=1.03 m²; Outside Heavy Duty Interlocker=No; Sash Height=807 mm  [stored 2.64764 ft]; Sash Width Left=1498 mm; Sash Width Right=1498 mm; Standard Interlocker=Yes; Width=2990 mm; Windload Design=1500 mm  [stored 4.92126 ft]
- Elite-3009OX-2000Pa: Area Left Sash Glazing=1.03 m²; Area Right Sash Glazing=1.03 m²; Clearvue SHGC Value=0.744; Clearvue U Value=5.75; Custom Windload=2000 mm  [stored 6.56168 ft]; Custom Window Height=890 mm  [stored 2.91995 ft]; Custom Window Width=2990 mm; Energy Advantage SHGC Value=0.66; Energy Advantage U Value=4.08; Height=890 mm  [stored 2.91995 ft]; Inside Heavy Duty Interlocker=No; Interlocker Configuration=0 mm  [stored 0 ft]; Intruderprufe LowE SHGC Value=0.619; Intruderprufe LowE U Value=3.98; Intruderprufe SHGC Value=0.706; Intruderprufe U Value=5.62; Limit Sash Width Left Max=1500 mm  [stored 4.92126 ft]; Limit Sash Width Left Min=1496 mm; Limit Window Width Max=2994 mm; Max Pane Area=1.03 m²; Outside Heavy Duty Interlocker=No; Sash Height=807 mm  [stored 2.64764 ft]; Sash Width Left=1498 mm; Sash Width Right=1498 mm; Standard Interlocker=Yes; Width=2990 mm; Windload Design=2000 mm  [stored 6.56168 ft]
- Elite-3012OX-1500Pa: Area Left Sash Glazing=1.46 m²; Area Right Sash Glazing=1.46 m²; Clearvue SHGC Value=0.764; Clearvue U Value=5.79; Custom Windload=1500 mm  [stored 4.92126 ft]; Custom Window Height=1190 mm  [stored 3.9042 ft]; Custom Window Width=2990 mm; Energy Advantage SHGC Value=0.684; Energy Advantage U Value=4.03; Height=1190 mm  [stored 3.9042 ft]; Inside Heavy Duty Interlocker=Yes; Interlocker Configuration=1 mm  [stored 0.00328084 ft]; Intruderprufe LowE SHGC Value=0.636; Intruderprufe LowE U Value=3.93; Intruderprufe SHGC Value=0.725; Intruderprufe U Value=5.66; Limit Sash Width Left Max=1500 mm  [stored 4.92126 ft]; Limit Sash Width Left Min=1496 mm; Limit Window Width Max=2994 mm; Max Pane Area=1.46 m²; Outside Heavy Duty Interlocker=No; Sash Height=1107 mm  [stored 3.63189 ft]; Sash Width Left=1498 mm; Sash Width Right=1498 mm; Standard Interlocker=No; Width=2990 mm; Windload Design=1500 mm  [stored 4.92126 ft]
- Elite-3012OX-2000Pa: Area Left Sash Glazing=1.46 m²; Area Right Sash Glazing=1.46 m²; Clearvue SHGC Value=0.764; Clearvue U Value=5.79; Custom Windload=2000 mm  [stored 6.56168 ft]; Custom Window Height=1190 mm  [stored 3.9042 ft]; Custom Window Width=2990 mm; Energy Advantage SHGC Value=0.684; Energy Advantage U Value=4.03; Height=1190 mm  [stored 3.9042 ft]; Inside Heavy Duty Interlocker=Yes; Interlocker Configuration=1 mm  [stored 0.00328084 ft]; Intruderprufe LowE SHGC Value=0.636; Intruderprufe LowE U Value=3.93; Intruderprufe SHGC Value=0.725; Intruderprufe U Value=5.66; Limit Sash Width Left Max=1500 mm  [stored 4.92126 ft]; Limit Sash Width Left Min=1496 mm; Limit Window Width Max=2994 mm; Max Pane Area=1.46 m²; Outside Heavy Duty Interlocker=No; Sash Height=1107 mm  [stored 3.63189 ft]; Sash Width Left=1498 mm; Sash Width Right=1498 mm; Standard Interlocker=No; Width=2990 mm; Windload Design=2000 mm  [stored 6.56168 ft]
- Elite-3015OX-1500Pa: Area Left Sash Glazing=1.89 m²; Area Right Sash Glazing=1.89 m²; Clearvue SHGC Value=0.777; Clearvue U Value=5.82; Custom Windload=1500 mm  [stored 4.92126 ft]; Custom Window Height=1490 mm  [stored 4.88845 ft]; Custom Window Width=2990 mm; Energy Advantage SHGC Value=0.695; Energy Advantage U Value=4; Height=1490 mm  [stored 4.88845 ft]; Inside Heavy Duty Interlocker=Yes; Interlocker Configuration=2 mm  [stored 0.00656168 ft]; Intruderprufe LowE SHGC Value=0.645; Intruderprufe LowE U Value=3.9; Intruderprufe SHGC Value=0.737; Intruderprufe U Value=5.69; Limit Sash Width Left Max=1500 mm  [stored 4.92126 ft]; Limit Sash Width Left Min=1496 mm; Limit Window Width Max=2994 mm; Max Pane Area=1.89 m²; Outside Heavy Duty Interlocker=Yes; Sash Height=1407 mm  [stored 4.61614 ft]; Sash Width Left=1498 mm; Sash Width Right=1498 mm; Standard Interlocker=No; Width=2990 mm; Windload Design=1500 mm  [stored 4.92126 ft]
- Elite-3015OX-2000Pa: Area Left Sash Glazing=1.89 m²; Area Right Sash Glazing=1.89 m²; Clearvue SHGC Value=0.777; Clearvue U Value=5.82; Custom Windload=2000 mm  [stored 6.56168 ft]; Custom Window Height=1490 mm  [stored 4.88845 ft]; Custom Window Width=2990 mm; Energy Advantage SHGC Value=0.695; Energy Advantage U Value=4; Height=1490 mm  [stored 4.88845 ft]; Inside Heavy Duty Interlocker=Yes; Interlocker Configuration=2 mm  [stored 0.00656168 ft]; Intruderprufe LowE SHGC Value=0.645; Intruderprufe LowE U Value=3.9; Intruderprufe SHGC Value=0.737; Intruderprufe U Value=5.69; Limit Sash Width Left Max=1500 mm  [stored 4.92126 ft]; Limit Sash Width Left Min=1496 mm; Limit Window Width Max=2994 mm; Max Pane Area=1.89 m²; Outside Heavy Duty Interlocker=Yes; Sash Height=1407 mm  [stored 4.61614 ft]; Sash Width Left=1498 mm; Sash Width Right=1498 mm; Standard Interlocker=No; Width=2990 mm; Windload Design=2000 mm  [stored 6.56168 ft]

note: [stored X ft] marks values corroborated as IEEE doubles in the binary element streams (Revit-internal decimal feet)

## geometry (parser evidence)
native form markers: Sweep x33
no freeform markers — native parametric forms only
